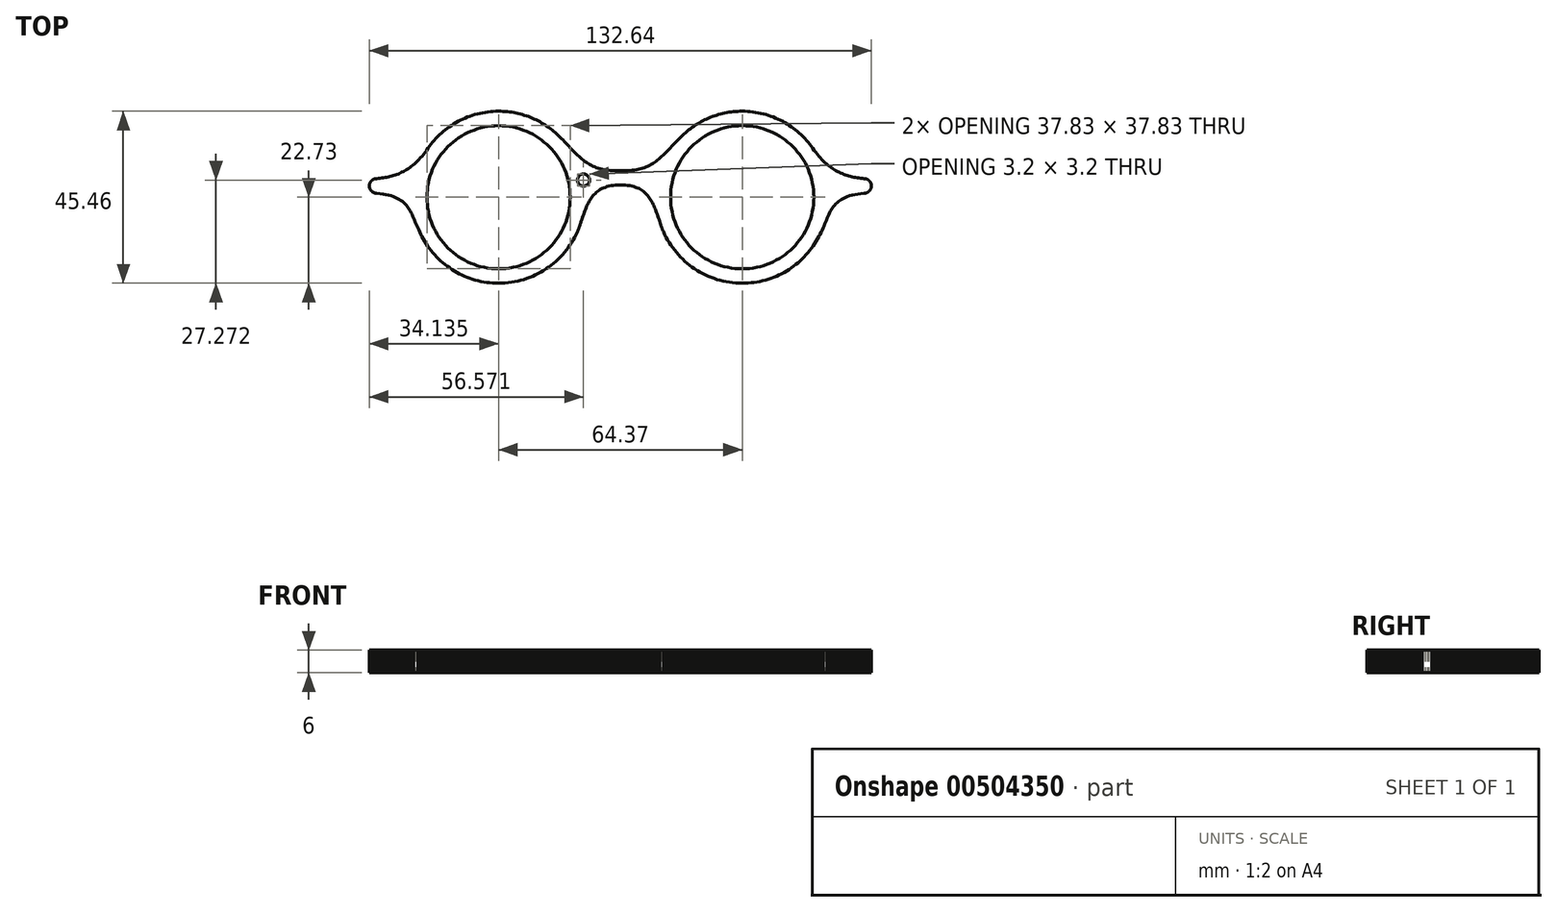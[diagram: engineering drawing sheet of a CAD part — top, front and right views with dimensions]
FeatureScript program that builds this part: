
annotation { "Feature Type Name" : "Feature", "Feature Type Description" : "" }
export const myFeature = defineFeature(function(context is Context, id is Id, definition is map)
    precondition{}
    {
        {
            var Q0;
            Q0=qCreatedBy(makeId("Top.planeOp"),FACE);
            var sketch = newSketch(context, id + "F0", { "sketchPlane" : qUnion([Q0])});
            skLineSegment(sketch, "E0", {"start": v(66.32, 3.1) * mm, "end": v(66.3, 3.2) * mm});
            skLineSegment(sketch, "E1", {"start": v(66.3, 3.2) * mm, "end": v(66.3, 3.3) * mm});
            skLineSegment(sketch, "E2", {"start": v(66.3, 3.3) * mm, "end": v(66.28, 3.39) * mm});
            skLineSegment(sketch, "E3", {"start": v(66.28, 3.39) * mm, "end": v(66.26, 3.48) * mm});
            skLineSegment(sketch, "E4", {"start": v(66.26, 3.48) * mm, "end": v(66.23, 3.57) * mm});
            skLineSegment(sketch, "E5", {"start": v(66.23, 3.57) * mm, "end": v(66.2, 3.66) * mm});
            skLineSegment(sketch, "E6", {"start": v(66.2, 3.66) * mm, "end": v(66.17, 3.75) * mm});
            skLineSegment(sketch, "E7", {"start": v(66.17, 3.75) * mm, "end": v(66.13, 3.84) * mm});
            skLineSegment(sketch, "E8", {"start": v(66.13, 3.84) * mm, "end": v(66.08, 3.92) * mm});
            skLineSegment(sketch, "E9", {"start": v(66.08, 3.92) * mm, "end": v(66.04, 4) * mm});
            skLineSegment(sketch, "E10", {"start": v(66.04, 4) * mm, "end": v(65.99, 4.08) * mm});
            skLineSegment(sketch, "E11", {"start": v(65.99, 4.08) * mm, "end": v(65.93, 4.16) * mm});
            skLineSegment(sketch, "E12", {"start": v(65.93, 4.16) * mm, "end": v(65.88, 4.23) * mm});
            skLineSegment(sketch, "E13", {"start": v(65.88, 4.23) * mm, "end": v(65.82, 4.3) * mm});
            skLineSegment(sketch, "E14", {"start": v(65.82, 4.3) * mm, "end": v(65.75, 4.37) * mm});
            skLineSegment(sketch, "E15", {"start": v(65.75, 4.37) * mm, "end": v(65.69, 4.43) * mm});
            skLineSegment(sketch, "E16", {"start": v(65.69, 4.43) * mm, "end": v(65.62, 4.5) * mm});
            skLineSegment(sketch, "E17", {"start": v(65.62, 4.5) * mm, "end": v(65.54, 4.55) * mm});
            skLineSegment(sketch, "E18", {"start": v(65.54, 4.55) * mm, "end": v(65.47, 4.6) * mm});
            skLineSegment(sketch, "E19", {"start": v(65.47, 4.6) * mm, "end": v(65.39, 4.65) * mm});
            skLineSegment(sketch, "E20", {"start": v(65.39, 4.65) * mm, "end": v(65.3, 4.7) * mm});
            skLineSegment(sketch, "E21", {"start": v(65.3, 4.7) * mm, "end": v(65.22, 4.74) * mm});
            skLineSegment(sketch, "E22", {"start": v(65.22, 4.74) * mm, "end": v(65.14, 4.78) * mm});
            skLineSegment(sketch, "E23", {"start": v(65.14, 4.78) * mm, "end": v(65.05, 4.81) * mm});
            skLineSegment(sketch, "E24", {"start": v(65.05, 4.81) * mm, "end": v(64.96, 4.84) * mm});
            skLineSegment(sketch, "E25", {"start": v(64.96, 4.84) * mm, "end": v(64.87, 4.87) * mm});
            skLineSegment(sketch, "E26", {"start": v(64.87, 4.87) * mm, "end": v(64.78, 4.9) * mm});
            skLineSegment(sketch, "E27", {"start": v(64.78, 4.9) * mm, "end": v(64.68, 4.9) * mm});
            skLineSegment(sketch, "E28", {"start": v(64.68, 4.9) * mm, "end": v(64.58, 4.92) * mm});
            skLineSegment(sketch, "E29", {"start": v(64.58, 4.92) * mm, "end": v(64.49, 4.93) * mm});
            skLineSegment(sketch, "E30", {"start": v(64.49, 4.93) * mm, "end": v(64.39, 4.93) * mm});
            skLineSegment(sketch, "E31", {"start": v(64.39, 4.93) * mm, "end": v(63.93, 4.97) * mm});
            skLineSegment(sketch, "E32", {"start": v(63.93, 4.97) * mm, "end": v(63.48, 5.02) * mm});
            skLineSegment(sketch, "E33", {"start": v(63.48, 5.02) * mm, "end": v(63.03, 5.07) * mm});
            skLineSegment(sketch, "E34", {"start": v(63.03, 5.07) * mm, "end": v(62.58, 5.14) * mm});
            skLineSegment(sketch, "E35", {"start": v(62.58, 5.14) * mm, "end": v(62.13, 5.21) * mm});
            skLineSegment(sketch, "E36", {"start": v(62.13, 5.21) * mm, "end": v(61.68, 5.3) * mm});
            skLineSegment(sketch, "E37", {"start": v(61.68, 5.3) * mm, "end": v(61.24, 5.4) * mm});
            skLineSegment(sketch, "E38", {"start": v(61.24, 5.4) * mm, "end": v(60.8, 5.5) * mm});
            skLineSegment(sketch, "E39", {"start": v(60.8, 5.5) * mm, "end": v(60.36, 5.61) * mm});
            skLineSegment(sketch, "E40", {"start": v(60.36, 5.61) * mm, "end": v(59.92, 5.74) * mm});
            skLineSegment(sketch, "E41", {"start": v(59.92, 5.74) * mm, "end": v(59.48, 5.89) * mm});
            skLineSegment(sketch, "E42", {"start": v(59.48, 5.89) * mm, "end": v(59.04, 6.04) * mm});
            skLineSegment(sketch, "E43", {"start": v(59.04, 6.04) * mm, "end": v(58.61, 6.22) * mm});
            skLineSegment(sketch, "E44", {"start": v(58.61, 6.22) * mm, "end": v(58.18, 6.4) * mm});
            skLineSegment(sketch, "E45", {"start": v(58.18, 6.4) * mm, "end": v(57.75, 6.6) * mm});
            skLineSegment(sketch, "E46", {"start": v(57.75, 6.6) * mm, "end": v(57.32, 6.82) * mm});
            skLineSegment(sketch, "E47", {"start": v(57.32, 6.82) * mm, "end": v(56.9, 7.06) * mm});
            skLineSegment(sketch, "E48", {"start": v(56.9, 7.06) * mm, "end": v(56.48, 7.3) * mm});
            skLineSegment(sketch, "E49", {"start": v(56.48, 7.3) * mm, "end": v(56.06, 7.58) * mm});
            skLineSegment(sketch, "E50", {"start": v(56.06, 7.58) * mm, "end": v(55.64, 7.86) * mm});
            skLineSegment(sketch, "E51", {"start": v(55.64, 7.86) * mm, "end": v(55.23, 8.17) * mm});
            skLineSegment(sketch, "E52", {"start": v(55.23, 8.17) * mm, "end": v(54.81, 8.5) * mm});
            skLineSegment(sketch, "E53", {"start": v(54.81, 8.5) * mm, "end": v(54.4, 8.84) * mm});
            skLineSegment(sketch, "E54", {"start": v(54.4, 8.84) * mm, "end": v(54, 9.21) * mm});
            skLineSegment(sketch, "E55", {"start": v(54, 9.21) * mm, "end": v(53.6, 9.6) * mm});
            skLineSegment(sketch, "E56", {"start": v(53.6, 9.6) * mm, "end": v(53.2, 10) * mm});
            skLineSegment(sketch, "E57", {"start": v(53.2, 10) * mm, "end": v(52.8, 10.44) * mm});
            skLineSegment(sketch, "E58", {"start": v(52.8, 10.44) * mm, "end": v(52.4, 10.9) * mm});
            skLineSegment(sketch, "E59", {"start": v(52.4, 10.9) * mm, "end": v(52, 11.38) * mm});
            skLineSegment(sketch, "E60", {"start": v(52, 11.38) * mm, "end": v(51.61, 11.88) * mm});
            skLineSegment(sketch, "E61", {"start": v(51.61, 11.88) * mm, "end": v(51.23, 12.41) * mm});
            skLineSegment(sketch, "E62", {"start": v(51.23, 12.41) * mm, "end": v(50.84, 12.97) * mm});
            skLineSegment(sketch, "E63", {"start": v(50.84, 12.97) * mm, "end": v(50.45, 13.51) * mm});
            skLineSegment(sketch, "E64", {"start": v(50.45, 13.51) * mm, "end": v(50.04, 14.05) * mm});
            skLineSegment(sketch, "E65", {"start": v(50.04, 14.05) * mm, "end": v(49.62, 14.57) * mm});
            skLineSegment(sketch, "E66", {"start": v(49.62, 14.57) * mm, "end": v(49.18, 15.08) * mm});
            skLineSegment(sketch, "E67", {"start": v(49.18, 15.08) * mm, "end": v(48.72, 15.58) * mm});
            skLineSegment(sketch, "E68", {"start": v(48.72, 15.58) * mm, "end": v(48.26, 16.06) * mm});
            skLineSegment(sketch, "E69", {"start": v(48.26, 16.06) * mm, "end": v(47.77, 16.53) * mm});
            skLineSegment(sketch, "E70", {"start": v(47.77, 16.53) * mm, "end": v(47.28, 16.98) * mm});
            skLineSegment(sketch, "E71", {"start": v(47.28, 16.98) * mm, "end": v(46.77, 17.42) * mm});
            skLineSegment(sketch, "E72", {"start": v(46.77, 17.42) * mm, "end": v(46.25, 17.85) * mm});
            skLineSegment(sketch, "E73", {"start": v(46.25, 17.85) * mm, "end": v(45.71, 18.26) * mm});
            skLineSegment(sketch, "E74", {"start": v(45.71, 18.26) * mm, "end": v(45.17, 18.65) * mm});
            skLineSegment(sketch, "E75", {"start": v(45.17, 18.65) * mm, "end": v(44.6, 19.03) * mm});
            skLineSegment(sketch, "E76", {"start": v(44.6, 19.03) * mm, "end": v(44.04, 19.39) * mm});
            skLineSegment(sketch, "E77", {"start": v(44.04, 19.39) * mm, "end": v(43.46, 19.73) * mm});
            skLineSegment(sketch, "E78", {"start": v(43.46, 19.73) * mm, "end": v(42.87, 20.06) * mm});
            skLineSegment(sketch, "E79", {"start": v(42.87, 20.06) * mm, "end": v(42.26, 20.37) * mm});
            skLineSegment(sketch, "E80", {"start": v(42.26, 20.37) * mm, "end": v(41.65, 20.67) * mm});
            skLineSegment(sketch, "E81", {"start": v(41.65, 20.67) * mm, "end": v(41.03, 20.94) * mm});
            skLineSegment(sketch, "E82", {"start": v(41.03, 20.94) * mm, "end": v(40.4, 21.2) * mm});
            skLineSegment(sketch, "E83", {"start": v(40.4, 21.2) * mm, "end": v(39.75, 21.44) * mm});
            skLineSegment(sketch, "E84", {"start": v(39.75, 21.44) * mm, "end": v(39.1, 21.66) * mm});
            skLineSegment(sketch, "E85", {"start": v(39.1, 21.66) * mm, "end": v(38.45, 21.86) * mm});
            skLineSegment(sketch, "E86", {"start": v(38.45, 21.86) * mm, "end": v(37.78, 22.04) * mm});
            skLineSegment(sketch, "E87", {"start": v(37.78, 22.04) * mm, "end": v(37.1, 22.2) * mm});
            skLineSegment(sketch, "E88", {"start": v(37.1, 22.2) * mm, "end": v(36.42, 22.34) * mm});
            skLineSegment(sketch, "E89", {"start": v(36.42, 22.34) * mm, "end": v(35.73, 22.46) * mm});
            skLineSegment(sketch, "E90", {"start": v(35.73, 22.46) * mm, "end": v(35.03, 22.56) * mm});
            skLineSegment(sketch, "E91", {"start": v(35.03, 22.56) * mm, "end": v(34.33, 22.63) * mm});
            skLineSegment(sketch, "E92", {"start": v(34.33, 22.63) * mm, "end": v(33.62, 22.69) * mm});
            skLineSegment(sketch, "E93", {"start": v(33.62, 22.69) * mm, "end": v(32.9, 22.72) * mm});
            skLineSegment(sketch, "E94", {"start": v(32.9, 22.72) * mm, "end": v(32.19, 22.73) * mm});
            skLineSegment(sketch, "E95", {"start": v(32.19, 22.73) * mm, "end": v(31.6, 22.73) * mm});
            skLineSegment(sketch, "E96", {"start": v(31.6, 22.73) * mm, "end": v(31, 22.7) * mm});
            skLineSegment(sketch, "E97", {"start": v(31, 22.7) * mm, "end": v(30.42, 22.67) * mm});
            skLineSegment(sketch, "E98", {"start": v(30.42, 22.67) * mm, "end": v(29.84, 22.61) * mm});
            skLineSegment(sketch, "E99", {"start": v(29.84, 22.61) * mm, "end": v(29.27, 22.55) * mm});
            skLineSegment(sketch, "E100", {"start": v(29.27, 22.55) * mm, "end": v(28.7, 22.47) * mm});
            skLineSegment(sketch, "E101", {"start": v(28.7, 22.47) * mm, "end": v(28.13, 22.37) * mm});
            skLineSegment(sketch, "E102", {"start": v(28.13, 22.37) * mm, "end": v(27.57, 22.26) * mm});
            skLineSegment(sketch, "E103", {"start": v(27.57, 22.26) * mm, "end": v(27.01, 22.14) * mm});
            skLineSegment(sketch, "E104", {"start": v(27.01, 22.14) * mm, "end": v(26.46, 22) * mm});
            skLineSegment(sketch, "E105", {"start": v(26.46, 22) * mm, "end": v(25.92, 21.85) * mm});
            skLineSegment(sketch, "E106", {"start": v(25.92, 21.85) * mm, "end": v(25.38, 21.7) * mm});
            skLineSegment(sketch, "E107", {"start": v(25.38, 21.7) * mm, "end": v(24.84, 21.52) * mm});
            skLineSegment(sketch, "E108", {"start": v(24.84, 21.52) * mm, "end": v(24.31, 21.33) * mm});
            skLineSegment(sketch, "E109", {"start": v(24.31, 21.33) * mm, "end": v(23.8, 21.13) * mm});
            skLineSegment(sketch, "E110", {"start": v(23.8, 21.13) * mm, "end": v(23.28, 20.91) * mm});
            skLineSegment(sketch, "E111", {"start": v(23.28, 20.91) * mm, "end": v(22.77, 20.69) * mm});
            skLineSegment(sketch, "E112", {"start": v(22.77, 20.69) * mm, "end": v(22.26, 20.45) * mm});
            skLineSegment(sketch, "E113", {"start": v(22.26, 20.45) * mm, "end": v(21.77, 20.2) * mm});
            skLineSegment(sketch, "E114", {"start": v(21.77, 20.2) * mm, "end": v(21.28, 19.94) * mm});
            skLineSegment(sketch, "E115", {"start": v(21.28, 19.94) * mm, "end": v(20.8, 19.67) * mm});
            skLineSegment(sketch, "E116", {"start": v(20.8, 19.67) * mm, "end": v(20.32, 19.38) * mm});
            skLineSegment(sketch, "E117", {"start": v(20.32, 19.38) * mm, "end": v(19.85, 19.09) * mm});
            skLineSegment(sketch, "E118", {"start": v(19.85, 19.09) * mm, "end": v(19.4, 18.78) * mm});
            skLineSegment(sketch, "E119", {"start": v(19.4, 18.78) * mm, "end": v(18.94, 18.46) * mm});
            skLineSegment(sketch, "E120", {"start": v(18.94, 18.46) * mm, "end": v(18.5, 18.14) * mm});
            skLineSegment(sketch, "E121", {"start": v(18.5, 18.14) * mm, "end": v(18.06, 17.8) * mm});
            skLineSegment(sketch, "E122", {"start": v(18.06, 17.8) * mm, "end": v(17.63, 17.45) * mm});
            skLineSegment(sketch, "E123", {"start": v(17.63, 17.45) * mm, "end": v(17.21, 17.1) * mm});
            skLineSegment(sketch, "E124", {"start": v(17.21, 17.1) * mm, "end": v(16.8, 16.72) * mm});
            skLineSegment(sketch, "E125", {"start": v(16.8, 16.72) * mm, "end": v(16.4, 16.35) * mm});
            skLineSegment(sketch, "E126", {"start": v(16.4, 16.35) * mm, "end": v(16.01, 15.96) * mm});
            skLineSegment(sketch, "E127", {"start": v(16.01, 15.96) * mm, "end": v(15.58, 15.53) * mm});
            skLineSegment(sketch, "E128", {"start": v(15.58, 15.53) * mm, "end": v(15.16, 15.11) * mm});
            skLineSegment(sketch, "E129", {"start": v(15.16, 15.11) * mm, "end": v(14.75, 14.7) * mm});
            skLineSegment(sketch, "E130", {"start": v(14.75, 14.7) * mm, "end": v(14.35, 14.27) * mm});
            skLineSegment(sketch, "E131", {"start": v(14.35, 14.27) * mm, "end": v(13.96, 13.86) * mm});
            skLineSegment(sketch, "E132", {"start": v(13.96, 13.86) * mm, "end": v(13.57, 13.45) * mm});
            skLineSegment(sketch, "E133", {"start": v(13.57, 13.45) * mm, "end": v(13.18, 13.05) * mm});
            skLineSegment(sketch, "E134", {"start": v(13.18, 13.05) * mm, "end": v(12.8, 12.66) * mm});
            skLineSegment(sketch, "E135", {"start": v(12.8, 12.66) * mm, "end": v(12.43, 12.27) * mm});
            skLineSegment(sketch, "E136", {"start": v(12.43, 12.27) * mm, "end": v(12.05, 11.89) * mm});
            skLineSegment(sketch, "E137", {"start": v(12.05, 11.89) * mm, "end": v(11.68, 11.52) * mm});
            skLineSegment(sketch, "E138", {"start": v(11.68, 11.52) * mm, "end": v(11.3, 11.15) * mm});
            skLineSegment(sketch, "E139", {"start": v(11.3, 11.15) * mm, "end": v(10.92, 10.8) * mm});
            skLineSegment(sketch, "E140", {"start": v(10.92, 10.8) * mm, "end": v(10.54, 10.46) * mm});
            skLineSegment(sketch, "E141", {"start": v(10.54, 10.46) * mm, "end": v(10.16, 10.13) * mm});
            skLineSegment(sketch, "E142", {"start": v(10.16, 10.13) * mm, "end": v(9.77, 9.81) * mm});
            skLineSegment(sketch, "E143", {"start": v(9.77, 9.81) * mm, "end": v(9.37, 9.5) * mm});
            skLineSegment(sketch, "E144", {"start": v(9.37, 9.5) * mm, "end": v(8.97, 9.22) * mm});
            skLineSegment(sketch, "E145", {"start": v(8.97, 9.22) * mm, "end": v(8.55, 8.94) * mm});
            skLineSegment(sketch, "E146", {"start": v(8.55, 8.94) * mm, "end": v(8.13, 8.68) * mm});
            skLineSegment(sketch, "E147", {"start": v(8.13, 8.68) * mm, "end": v(7.7, 8.44) * mm});
            skLineSegment(sketch, "E148", {"start": v(7.7, 8.44) * mm, "end": v(7.25, 8.22) * mm});
            skLineSegment(sketch, "E149", {"start": v(7.25, 8.22) * mm, "end": v(6.8, 8) * mm});
            skLineSegment(sketch, "E150", {"start": v(6.8, 8) * mm, "end": v(6.32, 7.82) * mm});
            skLineSegment(sketch, "E151", {"start": v(6.32, 7.82) * mm, "end": v(5.84, 7.65) * mm});
            skLineSegment(sketch, "E152", {"start": v(5.84, 7.65) * mm, "end": v(5.33, 7.5) * mm});
            skLineSegment(sketch, "E153", {"start": v(5.33, 7.5) * mm, "end": v(4.81, 7.37) * mm});
            skLineSegment(sketch, "E154", {"start": v(4.81, 7.37) * mm, "end": v(4.27, 7.26) * mm});
            skLineSegment(sketch, "E155", {"start": v(4.27, 7.26) * mm, "end": v(3.71, 7.18) * mm});
            skLineSegment(sketch, "E156", {"start": v(3.71, 7.18) * mm, "end": v(3.13, 7.12) * mm});
            skLineSegment(sketch, "E157", {"start": v(3.13, 7.12) * mm, "end": v(2.53, 7.08) * mm});
            skLineSegment(sketch, "E158", {"start": v(2.53, 7.08) * mm, "end": v(1.9, 7.07) * mm});
            skLineSegment(sketch, "E159", {"start": v(1.9, 7.07) * mm, "end": v(0, 7.07) * mm});
            skLineSegment(sketch, "E160", {"start": v(0, 7.07) * mm, "end": v(-1.9, 7.07) * mm});
            skLineSegment(sketch, "E161", {"start": v(-1.9, 7.07) * mm, "end": v(-2.52, 7.08) * mm});
            skLineSegment(sketch, "E162", {"start": v(-2.52, 7.08) * mm, "end": v(-3.13, 7.12) * mm});
            skLineSegment(sketch, "E163", {"start": v(-3.13, 7.12) * mm, "end": v(-3.71, 7.18) * mm});
            skLineSegment(sketch, "E164", {"start": v(-3.71, 7.18) * mm, "end": v(-4.27, 7.26) * mm});
            skLineSegment(sketch, "E165", {"start": v(-4.27, 7.26) * mm, "end": v(-4.81, 7.37) * mm});
            skLineSegment(sketch, "E166", {"start": v(-4.81, 7.37) * mm, "end": v(-5.33, 7.5) * mm});
            skLineSegment(sketch, "E167", {"start": v(-5.33, 7.5) * mm, "end": v(-5.84, 7.65) * mm});
            skLineSegment(sketch, "E168", {"start": v(-5.84, 7.65) * mm, "end": v(-6.32, 7.82) * mm});
            skLineSegment(sketch, "E169", {"start": v(-6.32, 7.82) * mm, "end": v(-6.8, 8) * mm});
            skLineSegment(sketch, "E170", {"start": v(-6.8, 8) * mm, "end": v(-7.25, 8.22) * mm});
            skLineSegment(sketch, "E171", {"start": v(-7.25, 8.22) * mm, "end": v(-7.7, 8.44) * mm});
            skLineSegment(sketch, "E172", {"start": v(-7.7, 8.44) * mm, "end": v(-8.13, 8.68) * mm});
            skLineSegment(sketch, "E173", {"start": v(-8.13, 8.68) * mm, "end": v(-8.55, 8.94) * mm});
            skLineSegment(sketch, "E174", {"start": v(-8.55, 8.94) * mm, "end": v(-8.97, 9.22) * mm});
            skLineSegment(sketch, "E175", {"start": v(-8.97, 9.22) * mm, "end": v(-9.37, 9.5) * mm});
            skLineSegment(sketch, "E176", {"start": v(-9.37, 9.5) * mm, "end": v(-9.77, 9.81) * mm});
            skLineSegment(sketch, "E177", {"start": v(-9.77, 9.81) * mm, "end": v(-10.16, 10.13) * mm});
            skLineSegment(sketch, "E178", {"start": v(-10.16, 10.13) * mm, "end": v(-10.54, 10.46) * mm});
            skLineSegment(sketch, "E179", {"start": v(-10.54, 10.46) * mm, "end": v(-10.92, 10.8) * mm});
            skLineSegment(sketch, "E180", {"start": v(-10.92, 10.8) * mm, "end": v(-11.3, 11.15) * mm});
            skLineSegment(sketch, "E181", {"start": v(-11.3, 11.15) * mm, "end": v(-11.68, 11.52) * mm});
            skLineSegment(sketch, "E182", {"start": v(-11.68, 11.52) * mm, "end": v(-12.05, 11.89) * mm});
            skLineSegment(sketch, "E183", {"start": v(-12.05, 11.89) * mm, "end": v(-12.43, 12.27) * mm});
            skLineSegment(sketch, "E184", {"start": v(-12.43, 12.27) * mm, "end": v(-12.8, 12.66) * mm});
            skLineSegment(sketch, "E185", {"start": v(-12.8, 12.66) * mm, "end": v(-13.18, 13.05) * mm});
            skLineSegment(sketch, "E186", {"start": v(-13.18, 13.05) * mm, "end": v(-13.57, 13.45) * mm});
            skLineSegment(sketch, "E187", {"start": v(-13.57, 13.45) * mm, "end": v(-13.96, 13.86) * mm});
            skLineSegment(sketch, "E188", {"start": v(-13.96, 13.86) * mm, "end": v(-14.35, 14.27) * mm});
            skLineSegment(sketch, "E189", {"start": v(-14.35, 14.27) * mm, "end": v(-14.75, 14.7) * mm});
            skLineSegment(sketch, "E190", {"start": v(-14.75, 14.7) * mm, "end": v(-15.16, 15.11) * mm});
            skLineSegment(sketch, "E191", {"start": v(-15.16, 15.11) * mm, "end": v(-15.58, 15.53) * mm});
            skLineSegment(sketch, "E192", {"start": v(-15.58, 15.53) * mm, "end": v(-16.01, 15.96) * mm});
            skLineSegment(sketch, "E193", {"start": v(-16.01, 15.96) * mm, "end": v(-16.4, 16.35) * mm});
            skLineSegment(sketch, "E194", {"start": v(-16.4, 16.35) * mm, "end": v(-16.8, 16.72) * mm});
            skLineSegment(sketch, "E195", {"start": v(-16.8, 16.72) * mm, "end": v(-17.21, 17.1) * mm});
            skLineSegment(sketch, "E196", {"start": v(-17.21, 17.1) * mm, "end": v(-17.63, 17.45) * mm});
            skLineSegment(sketch, "E197", {"start": v(-17.63, 17.45) * mm, "end": v(-18.06, 17.8) * mm});
            skLineSegment(sketch, "E198", {"start": v(-18.06, 17.8) * mm, "end": v(-18.5, 18.14) * mm});
            skLineSegment(sketch, "E199", {"start": v(-18.5, 18.14) * mm, "end": v(-18.94, 18.46) * mm});
            skLineSegment(sketch, "E200", {"start": v(-18.94, 18.46) * mm, "end": v(-19.4, 18.78) * mm});
            skLineSegment(sketch, "E201", {"start": v(-19.4, 18.78) * mm, "end": v(-19.85, 19.09) * mm});
            skLineSegment(sketch, "E202", {"start": v(-19.85, 19.09) * mm, "end": v(-20.32, 19.38) * mm});
            skLineSegment(sketch, "E203", {"start": v(-20.32, 19.38) * mm, "end": v(-20.8, 19.67) * mm});
            skLineSegment(sketch, "E204", {"start": v(-20.8, 19.67) * mm, "end": v(-21.28, 19.94) * mm});
            skLineSegment(sketch, "E205", {"start": v(-21.28, 19.94) * mm, "end": v(-21.77, 20.2) * mm});
            skLineSegment(sketch, "E206", {"start": v(-21.77, 20.2) * mm, "end": v(-22.26, 20.45) * mm});
            skLineSegment(sketch, "E207", {"start": v(-22.26, 20.45) * mm, "end": v(-22.76, 20.69) * mm});
            skLineSegment(sketch, "E208", {"start": v(-22.76, 20.69) * mm, "end": v(-23.27, 20.91) * mm});
            skLineSegment(sketch, "E209", {"start": v(-23.27, 20.91) * mm, "end": v(-23.8, 21.13) * mm});
            skLineSegment(sketch, "E210", {"start": v(-23.8, 21.13) * mm, "end": v(-24.31, 21.33) * mm});
            skLineSegment(sketch, "E211", {"start": v(-24.31, 21.33) * mm, "end": v(-24.84, 21.52) * mm});
            skLineSegment(sketch, "E212", {"start": v(-24.84, 21.52) * mm, "end": v(-25.38, 21.7) * mm});
            skLineSegment(sketch, "E213", {"start": v(-25.38, 21.7) * mm, "end": v(-25.92, 21.85) * mm});
            skLineSegment(sketch, "E214", {"start": v(-25.92, 21.85) * mm, "end": v(-26.46, 22) * mm});
            skLineSegment(sketch, "E215", {"start": v(-26.46, 22) * mm, "end": v(-27.01, 22.14) * mm});
            skLineSegment(sketch, "E216", {"start": v(-27.01, 22.14) * mm, "end": v(-27.57, 22.26) * mm});
            skLineSegment(sketch, "E217", {"start": v(-27.57, 22.26) * mm, "end": v(-28.13, 22.37) * mm});
            skLineSegment(sketch, "E218", {"start": v(-28.13, 22.37) * mm, "end": v(-28.7, 22.47) * mm});
            skLineSegment(sketch, "E219", {"start": v(-28.7, 22.47) * mm, "end": v(-29.27, 22.55) * mm});
            skLineSegment(sketch, "E220", {"start": v(-29.27, 22.55) * mm, "end": v(-29.84, 22.61) * mm});
            skLineSegment(sketch, "E221", {"start": v(-29.84, 22.61) * mm, "end": v(-30.42, 22.67) * mm});
            skLineSegment(sketch, "E222", {"start": v(-30.42, 22.67) * mm, "end": v(-31, 22.7) * mm});
            skLineSegment(sketch, "E223", {"start": v(-31, 22.7) * mm, "end": v(-31.6, 22.73) * mm});
            skLineSegment(sketch, "E224", {"start": v(-31.6, 22.73) * mm, "end": v(-32.19, 22.73) * mm});
            skLineSegment(sketch, "E225", {"start": v(-32.19, 22.73) * mm, "end": v(-32.9, 22.72) * mm});
            skLineSegment(sketch, "E226", {"start": v(-32.9, 22.72) * mm, "end": v(-33.62, 22.69) * mm});
            skLineSegment(sketch, "E227", {"start": v(-33.62, 22.69) * mm, "end": v(-34.33, 22.63) * mm});
            skLineSegment(sketch, "E228", {"start": v(-34.33, 22.63) * mm, "end": v(-35.03, 22.56) * mm});
            skLineSegment(sketch, "E229", {"start": v(-35.03, 22.56) * mm, "end": v(-35.73, 22.46) * mm});
            skLineSegment(sketch, "E230", {"start": v(-35.73, 22.46) * mm, "end": v(-36.42, 22.34) * mm});
            skLineSegment(sketch, "E231", {"start": v(-36.42, 22.34) * mm, "end": v(-37.1, 22.2) * mm});
            skLineSegment(sketch, "E232", {"start": v(-37.1, 22.2) * mm, "end": v(-37.78, 22.04) * mm});
            skLineSegment(sketch, "E233", {"start": v(-37.78, 22.04) * mm, "end": v(-38.45, 21.86) * mm});
            skLineSegment(sketch, "E234", {"start": v(-38.45, 21.86) * mm, "end": v(-39.1, 21.66) * mm});
            skLineSegment(sketch, "E235", {"start": v(-39.1, 21.66) * mm, "end": v(-39.75, 21.44) * mm});
            skLineSegment(sketch, "E236", {"start": v(-39.75, 21.44) * mm, "end": v(-40.4, 21.2) * mm});
            skLineSegment(sketch, "E237", {"start": v(-40.4, 21.2) * mm, "end": v(-41.03, 20.94) * mm});
            skLineSegment(sketch, "E238", {"start": v(-41.03, 20.94) * mm, "end": v(-41.65, 20.67) * mm});
            skLineSegment(sketch, "E239", {"start": v(-41.65, 20.67) * mm, "end": v(-42.26, 20.37) * mm});
            skLineSegment(sketch, "E240", {"start": v(-42.26, 20.37) * mm, "end": v(-42.87, 20.06) * mm});
            skLineSegment(sketch, "E241", {"start": v(-42.87, 20.06) * mm, "end": v(-43.46, 19.73) * mm});
            skLineSegment(sketch, "E242", {"start": v(-43.46, 19.73) * mm, "end": v(-44.04, 19.39) * mm});
            skLineSegment(sketch, "E243", {"start": v(-44.04, 19.39) * mm, "end": v(-44.6, 19.03) * mm});
            skLineSegment(sketch, "E244", {"start": v(-44.6, 19.03) * mm, "end": v(-45.17, 18.65) * mm});
            skLineSegment(sketch, "E245", {"start": v(-45.17, 18.65) * mm, "end": v(-45.71, 18.26) * mm});
            skLineSegment(sketch, "E246", {"start": v(-45.71, 18.26) * mm, "end": v(-46.25, 17.85) * mm});
            skLineSegment(sketch, "E247", {"start": v(-46.25, 17.85) * mm, "end": v(-46.77, 17.42) * mm});
            skLineSegment(sketch, "E248", {"start": v(-46.77, 17.42) * mm, "end": v(-47.28, 16.98) * mm});
            skLineSegment(sketch, "E249", {"start": v(-47.28, 16.98) * mm, "end": v(-47.77, 16.53) * mm});
            skLineSegment(sketch, "E250", {"start": v(-47.77, 16.53) * mm, "end": v(-48.25, 16.06) * mm});
            skLineSegment(sketch, "E251", {"start": v(-48.25, 16.06) * mm, "end": v(-48.72, 15.58) * mm});
            skLineSegment(sketch, "E252", {"start": v(-48.72, 15.58) * mm, "end": v(-49.18, 15.08) * mm});
            skLineSegment(sketch, "E253", {"start": v(-49.18, 15.08) * mm, "end": v(-49.62, 14.57) * mm});
            skLineSegment(sketch, "E254", {"start": v(-49.62, 14.57) * mm, "end": v(-50.04, 14.05) * mm});
            skLineSegment(sketch, "E255", {"start": v(-50.04, 14.05) * mm, "end": v(-50.45, 13.51) * mm});
            skLineSegment(sketch, "E256", {"start": v(-50.45, 13.51) * mm, "end": v(-50.84, 12.97) * mm});
            skLineSegment(sketch, "E257", {"start": v(-50.84, 12.97) * mm, "end": v(-51.23, 12.41) * mm});
            skLineSegment(sketch, "E258", {"start": v(-51.23, 12.41) * mm, "end": v(-51.61, 11.88) * mm});
            skLineSegment(sketch, "E259", {"start": v(-51.61, 11.88) * mm, "end": v(-52, 11.38) * mm});
            skLineSegment(sketch, "E260", {"start": v(-52, 11.38) * mm, "end": v(-52.4, 10.9) * mm});
            skLineSegment(sketch, "E261", {"start": v(-52.4, 10.9) * mm, "end": v(-52.8, 10.44) * mm});
            skLineSegment(sketch, "E262", {"start": v(-52.8, 10.44) * mm, "end": v(-53.2, 10) * mm});
            skLineSegment(sketch, "E263", {"start": v(-53.2, 10) * mm, "end": v(-53.6, 9.6) * mm});
            skLineSegment(sketch, "E264", {"start": v(-53.6, 9.6) * mm, "end": v(-54, 9.2) * mm});
            skLineSegment(sketch, "E265", {"start": v(-54, 9.2) * mm, "end": v(-54.4, 8.84) * mm});
            skLineSegment(sketch, "E266", {"start": v(-54.4, 8.84) * mm, "end": v(-54.82, 8.5) * mm});
            skLineSegment(sketch, "E267", {"start": v(-54.82, 8.5) * mm, "end": v(-55.23, 8.17) * mm});
            skLineSegment(sketch, "E268", {"start": v(-55.23, 8.17) * mm, "end": v(-55.64, 7.86) * mm});
            skLineSegment(sketch, "E269", {"start": v(-55.64, 7.86) * mm, "end": v(-56.06, 7.57) * mm});
            skLineSegment(sketch, "E270", {"start": v(-56.06, 7.57) * mm, "end": v(-56.48, 7.3) * mm});
            skLineSegment(sketch, "E271", {"start": v(-56.48, 7.3) * mm, "end": v(-56.9, 7.05) * mm});
            skLineSegment(sketch, "E272", {"start": v(-56.9, 7.05) * mm, "end": v(-57.33, 6.82) * mm});
            skLineSegment(sketch, "E273", {"start": v(-57.33, 6.82) * mm, "end": v(-57.76, 6.6) * mm});
            skLineSegment(sketch, "E274", {"start": v(-57.76, 6.6) * mm, "end": v(-58.19, 6.4) * mm});
            skLineSegment(sketch, "E275", {"start": v(-58.19, 6.4) * mm, "end": v(-58.62, 6.2) * mm});
            skLineSegment(sketch, "E276", {"start": v(-58.62, 6.2) * mm, "end": v(-59.05, 6.04) * mm});
            skLineSegment(sketch, "E277", {"start": v(-59.05, 6.04) * mm, "end": v(-59.49, 5.88) * mm});
            skLineSegment(sketch, "E278", {"start": v(-59.49, 5.88) * mm, "end": v(-59.93, 5.74) * mm});
            skLineSegment(sketch, "E279", {"start": v(-59.93, 5.74) * mm, "end": v(-60.36, 5.6) * mm});
            skLineSegment(sketch, "E280", {"start": v(-60.36, 5.6) * mm, "end": v(-60.8, 5.49) * mm});
            skLineSegment(sketch, "E281", {"start": v(-60.8, 5.49) * mm, "end": v(-61.25, 5.38) * mm});
            skLineSegment(sketch, "E282", {"start": v(-61.25, 5.38) * mm, "end": v(-61.7, 5.29) * mm});
            skLineSegment(sketch, "E283", {"start": v(-61.7, 5.29) * mm, "end": v(-62.14, 5.2) * mm});
            skLineSegment(sketch, "E284", {"start": v(-62.14, 5.2) * mm, "end": v(-62.58, 5.13) * mm});
            skLineSegment(sketch, "E285", {"start": v(-62.58, 5.13) * mm, "end": v(-63.03, 5.07) * mm});
            skLineSegment(sketch, "E286", {"start": v(-63.03, 5.07) * mm, "end": v(-63.48, 5.01) * mm});
            skLineSegment(sketch, "E287", {"start": v(-63.48, 5.01) * mm, "end": v(-63.93, 4.97) * mm});
            skLineSegment(sketch, "E288", {"start": v(-63.93, 4.97) * mm, "end": v(-64.39, 4.93) * mm});
            skLineSegment(sketch, "E289", {"start": v(-64.39, 4.93) * mm, "end": v(-64.49, 4.93) * mm});
            skLineSegment(sketch, "E290", {"start": v(-64.49, 4.93) * mm, "end": v(-64.58, 4.92) * mm});
            skLineSegment(sketch, "E291", {"start": v(-64.58, 4.92) * mm, "end": v(-64.68, 4.9) * mm});
            skLineSegment(sketch, "E292", {"start": v(-64.68, 4.9) * mm, "end": v(-64.78, 4.9) * mm});
            skLineSegment(sketch, "E293", {"start": v(-64.78, 4.9) * mm, "end": v(-64.87, 4.87) * mm});
            skLineSegment(sketch, "E294", {"start": v(-64.87, 4.87) * mm, "end": v(-64.96, 4.84) * mm});
            skLineSegment(sketch, "E295", {"start": v(-64.96, 4.84) * mm, "end": v(-65.05, 4.81) * mm});
            skLineSegment(sketch, "E296", {"start": v(-65.05, 4.81) * mm, "end": v(-65.14, 4.78) * mm});
            skLineSegment(sketch, "E297", {"start": v(-65.14, 4.78) * mm, "end": v(-65.22, 4.74) * mm});
            skLineSegment(sketch, "E298", {"start": v(-65.22, 4.74) * mm, "end": v(-65.3, 4.7) * mm});
            skLineSegment(sketch, "E299", {"start": v(-65.3, 4.7) * mm, "end": v(-65.39, 4.65) * mm});
            skLineSegment(sketch, "E300", {"start": v(-65.39, 4.65) * mm, "end": v(-65.47, 4.6) * mm});
            skLineSegment(sketch, "E301", {"start": v(-65.47, 4.6) * mm, "end": v(-65.54, 4.55) * mm});
            skLineSegment(sketch, "E302", {"start": v(-65.54, 4.55) * mm, "end": v(-65.62, 4.5) * mm});
            skLineSegment(sketch, "E303", {"start": v(-65.62, 4.5) * mm, "end": v(-65.69, 4.43) * mm});
            skLineSegment(sketch, "E304", {"start": v(-65.69, 4.43) * mm, "end": v(-65.75, 4.37) * mm});
            skLineSegment(sketch, "E305", {"start": v(-65.75, 4.37) * mm, "end": v(-65.82, 4.3) * mm});
            skLineSegment(sketch, "E306", {"start": v(-65.82, 4.3) * mm, "end": v(-65.88, 4.23) * mm});
            skLineSegment(sketch, "E307", {"start": v(-65.88, 4.23) * mm, "end": v(-65.93, 4.16) * mm});
            skLineSegment(sketch, "E308", {"start": v(-65.93, 4.16) * mm, "end": v(-65.99, 4.08) * mm});
            skLineSegment(sketch, "E309", {"start": v(-65.99, 4.08) * mm, "end": v(-66.04, 4) * mm});
            skLineSegment(sketch, "E310", {"start": v(-66.04, 4) * mm, "end": v(-66.08, 3.92) * mm});
            skLineSegment(sketch, "E311", {"start": v(-66.08, 3.92) * mm, "end": v(-66.13, 3.84) * mm});
            skLineSegment(sketch, "E312", {"start": v(-66.13, 3.84) * mm, "end": v(-66.17, 3.75) * mm});
            skLineSegment(sketch, "E313", {"start": v(-66.17, 3.75) * mm, "end": v(-66.2, 3.66) * mm});
            skLineSegment(sketch, "E314", {"start": v(-66.2, 3.66) * mm, "end": v(-66.23, 3.57) * mm});
            skLineSegment(sketch, "E315", {"start": v(-66.23, 3.57) * mm, "end": v(-66.26, 3.48) * mm});
            skLineSegment(sketch, "E316", {"start": v(-66.26, 3.48) * mm, "end": v(-66.28, 3.39) * mm});
            skLineSegment(sketch, "E317", {"start": v(-66.28, 3.39) * mm, "end": v(-66.3, 3.3) * mm});
            skLineSegment(sketch, "E318", {"start": v(-66.3, 3.3) * mm, "end": v(-66.3, 3.2) * mm});
            skLineSegment(sketch, "E319", {"start": v(-66.3, 3.2) * mm, "end": v(-66.32, 3.1) * mm});
            skLineSegment(sketch, "E320", {"start": v(-66.32, 3.1) * mm, "end": v(-66.32, 3) * mm});
            skLineSegment(sketch, "E321", {"start": v(-66.32, 3) * mm, "end": v(-66.32, 2.9) * mm});
            skLineSegment(sketch, "E322", {"start": v(-66.32, 2.9) * mm, "end": v(-66.3, 2.8) * mm});
            skLineSegment(sketch, "E323", {"start": v(-66.3, 2.8) * mm, "end": v(-66.3, 2.7) * mm});
            skLineSegment(sketch, "E324", {"start": v(-66.3, 2.7) * mm, "end": v(-66.28, 2.61) * mm});
            skLineSegment(sketch, "E325", {"start": v(-66.28, 2.61) * mm, "end": v(-66.26, 2.52) * mm});
            skLineSegment(sketch, "E326", {"start": v(-66.26, 2.52) * mm, "end": v(-66.23, 2.43) * mm});
            skLineSegment(sketch, "E327", {"start": v(-66.23, 2.43) * mm, "end": v(-66.2, 2.34) * mm});
            skLineSegment(sketch, "E328", {"start": v(-66.2, 2.34) * mm, "end": v(-66.17, 2.25) * mm});
            skLineSegment(sketch, "E329", {"start": v(-66.17, 2.25) * mm, "end": v(-66.13, 2.16) * mm});
            skLineSegment(sketch, "E330", {"start": v(-66.13, 2.16) * mm, "end": v(-66.08, 2.08) * mm});
            skLineSegment(sketch, "E331", {"start": v(-66.08, 2.08) * mm, "end": v(-66.04, 2) * mm});
            skLineSegment(sketch, "E332", {"start": v(-66.04, 2) * mm, "end": v(-65.99, 1.92) * mm});
            skLineSegment(sketch, "E333", {"start": v(-65.99, 1.92) * mm, "end": v(-65.93, 1.85) * mm});
            skLineSegment(sketch, "E334", {"start": v(-65.93, 1.85) * mm, "end": v(-65.88, 1.77) * mm});
            skLineSegment(sketch, "E335", {"start": v(-65.88, 1.77) * mm, "end": v(-65.82, 1.7) * mm});
            skLineSegment(sketch, "E336", {"start": v(-65.82, 1.7) * mm, "end": v(-65.75, 1.64) * mm});
            skLineSegment(sketch, "E337", {"start": v(-65.75, 1.64) * mm, "end": v(-65.69, 1.57) * mm});
            skLineSegment(sketch, "E338", {"start": v(-65.69, 1.57) * mm, "end": v(-65.62, 1.51) * mm});
            skLineSegment(sketch, "E339", {"start": v(-65.62, 1.51) * mm, "end": v(-65.54, 1.45) * mm});
            skLineSegment(sketch, "E340", {"start": v(-65.54, 1.45) * mm, "end": v(-65.47, 1.4) * mm});
            skLineSegment(sketch, "E341", {"start": v(-65.47, 1.4) * mm, "end": v(-65.39, 1.35) * mm});
            skLineSegment(sketch, "E342", {"start": v(-65.39, 1.35) * mm, "end": v(-65.3, 1.3) * mm});
            skLineSegment(sketch, "E343", {"start": v(-65.3, 1.3) * mm, "end": v(-65.22, 1.26) * mm});
            skLineSegment(sketch, "E344", {"start": v(-65.22, 1.26) * mm, "end": v(-65.14, 1.22) * mm});
            skLineSegment(sketch, "E345", {"start": v(-65.14, 1.22) * mm, "end": v(-65.05, 1.19) * mm});
            skLineSegment(sketch, "E346", {"start": v(-65.05, 1.19) * mm, "end": v(-64.96, 1.16) * mm});
            skLineSegment(sketch, "E347", {"start": v(-64.96, 1.16) * mm, "end": v(-64.87, 1.13) * mm});
            skLineSegment(sketch, "E348", {"start": v(-64.87, 1.13) * mm, "end": v(-64.78, 1.1) * mm});
            skLineSegment(sketch, "E349", {"start": v(-64.78, 1.1) * mm, "end": v(-64.68, 1.1) * mm});
            skLineSegment(sketch, "E350", {"start": v(-64.68, 1.1) * mm, "end": v(-64.58, 1.08) * mm});
            skLineSegment(sketch, "E351", {"start": v(-64.58, 1.08) * mm, "end": v(-64.49, 1.07) * mm});
            skLineSegment(sketch, "E352", {"start": v(-64.49, 1.07) * mm, "end": v(-64.39, 1.07) * mm});
            skLineSegment(sketch, "E353", {"start": v(-64.39, 1.07) * mm, "end": v(-64.39, 1.07) * mm});
            skLineSegment(sketch, "E354", {"start": v(-64.39, 1.07) * mm, "end": v(-63.5, 0.98) * mm});
            skLineSegment(sketch, "E355", {"start": v(-63.5, 0.98) * mm, "end": v(-62.7, 0.86) * mm});
            skLineSegment(sketch, "E356", {"start": v(-62.7, 0.86) * mm, "end": v(-61.93, 0.73) * mm});
            skLineSegment(sketch, "E357", {"start": v(-61.93, 0.73) * mm, "end": v(-61.23, 0.57) * mm});
            skLineSegment(sketch, "E358", {"start": v(-61.23, 0.57) * mm, "end": v(-60.58, 0.4) * mm});
            skLineSegment(sketch, "E359", {"start": v(-60.58, 0.4) * mm, "end": v(-59.97, 0.2) * mm});
            skLineSegment(sketch, "E360", {"start": v(-59.97, 0.2) * mm, "end": v(-59.41, -0.03) * mm});
            skLineSegment(sketch, "E361", {"start": v(-59.41, -0.03) * mm, "end": v(-58.9, -0.27) * mm});
            skLineSegment(sketch, "E362", {"start": v(-58.9, -0.27) * mm, "end": v(-58.43, -0.53) * mm});
            skLineSegment(sketch, "E363", {"start": v(-58.43, -0.53) * mm, "end": v(-58, -0.8) * mm});
            skLineSegment(sketch, "E364", {"start": v(-58, -0.8) * mm, "end": v(-57.59, -1.1) * mm});
            skLineSegment(sketch, "E365", {"start": v(-57.59, -1.1) * mm, "end": v(-57.22, -1.42) * mm});
            skLineSegment(sketch, "E366", {"start": v(-57.22, -1.42) * mm, "end": v(-56.88, -1.75) * mm});
            skLineSegment(sketch, "E367", {"start": v(-56.88, -1.75) * mm, "end": v(-56.56, -2.1) * mm});
            skLineSegment(sketch, "E368", {"start": v(-56.56, -2.1) * mm, "end": v(-56.27, -2.47) * mm});
            skLineSegment(sketch, "E369", {"start": v(-56.27, -2.47) * mm, "end": v(-56, -2.86) * mm});
            skLineSegment(sketch, "E370", {"start": v(-56, -2.86) * mm, "end": v(-55.75, -3.26) * mm});
            skLineSegment(sketch, "E371", {"start": v(-55.75, -3.26) * mm, "end": v(-55.5, -3.68) * mm});
            skLineSegment(sketch, "E372", {"start": v(-55.5, -3.68) * mm, "end": v(-55.28, -4.1) * mm});
            skLineSegment(sketch, "E373", {"start": v(-55.28, -4.1) * mm, "end": v(-55.06, -4.56) * mm});
            skLineSegment(sketch, "E374", {"start": v(-55.06, -4.56) * mm, "end": v(-54.85, -5.02) * mm});
            skLineSegment(sketch, "E375", {"start": v(-54.85, -5.02) * mm, "end": v(-54.64, -5.5) * mm});
            skLineSegment(sketch, "E376", {"start": v(-54.64, -5.5) * mm, "end": v(-54.43, -5.99) * mm});
            skLineSegment(sketch, "E377", {"start": v(-54.43, -5.99) * mm, "end": v(-54.22, -6.5) * mm});
            skLineSegment(sketch, "E378", {"start": v(-54.22, -6.5) * mm, "end": v(-54, -7.01) * mm});
            skLineSegment(sketch, "E379", {"start": v(-54, -7.01) * mm, "end": v(-53.77, -7.55) * mm});
            skLineSegment(sketch, "E380", {"start": v(-53.77, -7.55) * mm, "end": v(-53.54, -8.1) * mm});
            skLineSegment(sketch, "E381", {"start": v(-53.54, -8.1) * mm, "end": v(-53.28, -8.65) * mm});
            skLineSegment(sketch, "E382", {"start": v(-53.28, -8.65) * mm, "end": v(-53.02, -9.21) * mm});
            skLineSegment(sketch, "E383", {"start": v(-53.02, -9.21) * mm, "end": v(-52.73, -9.8) * mm});
            skLineSegment(sketch, "E384", {"start": v(-52.73, -9.8) * mm, "end": v(-52.42, -10.38) * mm});
            skLineSegment(sketch, "E385", {"start": v(-52.42, -10.38) * mm, "end": v(-52.08, -10.99) * mm});
            skLineSegment(sketch, "E386", {"start": v(-52.08, -10.99) * mm, "end": v(-51.7, -11.63) * mm});
            skLineSegment(sketch, "E387", {"start": v(-51.7, -11.63) * mm, "end": v(-51.31, -12.27) * mm});
            skLineSegment(sketch, "E388", {"start": v(-51.31, -12.27) * mm, "end": v(-50.9, -12.9) * mm});
            skLineSegment(sketch, "E389", {"start": v(-50.9, -12.9) * mm, "end": v(-50.46, -13.5) * mm});
            skLineSegment(sketch, "E390", {"start": v(-50.46, -13.5) * mm, "end": v(-50, -14.1) * mm});
            skLineSegment(sketch, "E391", {"start": v(-50, -14.1) * mm, "end": v(-49.54, -14.67) * mm});
            skLineSegment(sketch, "E392", {"start": v(-49.54, -14.67) * mm, "end": v(-49.05, -15.23) * mm});
            skLineSegment(sketch, "E393", {"start": v(-49.05, -15.23) * mm, "end": v(-48.54, -15.77) * mm});
            skLineSegment(sketch, "E394", {"start": v(-48.54, -15.77) * mm, "end": v(-48.01, -16.3) * mm});
            skLineSegment(sketch, "E395", {"start": v(-48.01, -16.3) * mm, "end": v(-47.47, -16.81) * mm});
            skLineSegment(sketch, "E396", {"start": v(-47.47, -16.81) * mm, "end": v(-46.91, -17.3) * mm});
            skLineSegment(sketch, "E397", {"start": v(-46.91, -17.3) * mm, "end": v(-46.34, -17.78) * mm});
            skLineSegment(sketch, "E398", {"start": v(-46.34, -17.78) * mm, "end": v(-45.75, -18.23) * mm});
            skLineSegment(sketch, "E399", {"start": v(-45.75, -18.23) * mm, "end": v(-45.14, -18.67) * mm});
            skLineSegment(sketch, "E400", {"start": v(-45.14, -18.67) * mm, "end": v(-44.52, -19.09) * mm});
            skLineSegment(sketch, "E401", {"start": v(-44.52, -19.09) * mm, "end": v(-43.89, -19.48) * mm});
            skLineSegment(sketch, "E402", {"start": v(-43.89, -19.48) * mm, "end": v(-43.24, -19.86) * mm});
            skLineSegment(sketch, "E403", {"start": v(-43.24, -19.86) * mm, "end": v(-42.58, -20.22) * mm});
            skLineSegment(sketch, "E404", {"start": v(-42.58, -20.22) * mm, "end": v(-41.9, -20.55) * mm});
            skLineSegment(sketch, "E405", {"start": v(-41.9, -20.55) * mm, "end": v(-41.22, -20.86) * mm});
            skLineSegment(sketch, "E406", {"start": v(-41.22, -20.86) * mm, "end": v(-40.52, -21.15) * mm});
            skLineSegment(sketch, "E407", {"start": v(-40.52, -21.15) * mm, "end": v(-39.8, -21.42) * mm});
            skLineSegment(sketch, "E408", {"start": v(-39.8, -21.42) * mm, "end": v(-39.09, -21.66) * mm});
            skLineSegment(sketch, "E409", {"start": v(-39.09, -21.66) * mm, "end": v(-38.36, -21.88) * mm});
            skLineSegment(sketch, "E410", {"start": v(-38.36, -21.88) * mm, "end": v(-37.62, -22.08) * mm});
            skLineSegment(sketch, "E411", {"start": v(-37.62, -22.08) * mm, "end": v(-36.86, -22.25) * mm});
            skLineSegment(sketch, "E412", {"start": v(-36.86, -22.25) * mm, "end": v(-36.1, -22.4) * mm});
            skLineSegment(sketch, "E413", {"start": v(-36.1, -22.4) * mm, "end": v(-35.34, -22.52) * mm});
            skLineSegment(sketch, "E414", {"start": v(-35.34, -22.52) * mm, "end": v(-34.56, -22.61) * mm});
            skLineSegment(sketch, "E415", {"start": v(-34.56, -22.61) * mm, "end": v(-33.78, -22.68) * mm});
            skLineSegment(sketch, "E416", {"start": v(-33.78, -22.68) * mm, "end": v(-32.98, -22.72) * mm});
            skLineSegment(sketch, "E417", {"start": v(-32.98, -22.72) * mm, "end": v(-32.19, -22.73) * mm});
            skLineSegment(sketch, "E418", {"start": v(-32.19, -22.73) * mm, "end": v(-31.32, -22.72) * mm});
            skLineSegment(sketch, "E419", {"start": v(-31.32, -22.72) * mm, "end": v(-30.46, -22.67) * mm});
            skLineSegment(sketch, "E420", {"start": v(-30.46, -22.67) * mm, "end": v(-29.6, -22.59) * mm});
            skLineSegment(sketch, "E421", {"start": v(-29.6, -22.59) * mm, "end": v(-28.76, -22.48) * mm});
            skLineSegment(sketch, "E422", {"start": v(-28.76, -22.48) * mm, "end": v(-27.93, -22.33) * mm});
            skLineSegment(sketch, "E423", {"start": v(-27.93, -22.33) * mm, "end": v(-27.11, -22.16) * mm});
            skLineSegment(sketch, "E424", {"start": v(-27.11, -22.16) * mm, "end": v(-26.3, -21.96) * mm});
            skLineSegment(sketch, "E425", {"start": v(-26.3, -21.96) * mm, "end": v(-25.5, -21.73) * mm});
            skLineSegment(sketch, "E426", {"start": v(-25.5, -21.73) * mm, "end": v(-24.71, -21.47) * mm});
            skLineSegment(sketch, "E427", {"start": v(-24.71, -21.47) * mm, "end": v(-23.94, -21.19) * mm});
            skLineSegment(sketch, "E428", {"start": v(-23.94, -21.19) * mm, "end": v(-23.18, -20.87) * mm});
            skLineSegment(sketch, "E429", {"start": v(-23.18, -20.87) * mm, "end": v(-22.43, -20.53) * mm});
            skLineSegment(sketch, "E430", {"start": v(-22.43, -20.53) * mm, "end": v(-21.7, -20.17) * mm});
            skLineSegment(sketch, "E431", {"start": v(-21.7, -20.17) * mm, "end": v(-20.99, -19.78) * mm});
            skLineSegment(sketch, "E432", {"start": v(-20.99, -19.78) * mm, "end": v(-20.29, -19.36) * mm});
            skLineSegment(sketch, "E433", {"start": v(-20.29, -19.36) * mm, "end": v(-19.6, -18.92) * mm});
            skLineSegment(sketch, "E434", {"start": v(-19.6, -18.92) * mm, "end": v(-18.93, -18.46) * mm});
            skLineSegment(sketch, "E435", {"start": v(-18.93, -18.46) * mm, "end": v(-18.28, -17.97) * mm});
            skLineSegment(sketch, "E436", {"start": v(-18.28, -17.97) * mm, "end": v(-17.65, -17.47) * mm});
            skLineSegment(sketch, "E437", {"start": v(-17.65, -17.47) * mm, "end": v(-17.04, -16.94) * mm});
            skLineSegment(sketch, "E438", {"start": v(-17.04, -16.94) * mm, "end": v(-16.45, -16.39) * mm});
            skLineSegment(sketch, "E439", {"start": v(-16.45, -16.39) * mm, "end": v(-15.87, -15.81) * mm});
            skLineSegment(sketch, "E440", {"start": v(-15.87, -15.81) * mm, "end": v(-15.32, -15.22) * mm});
            skLineSegment(sketch, "E441", {"start": v(-15.32, -15.22) * mm, "end": v(-14.79, -14.61) * mm});
            skLineSegment(sketch, "E442", {"start": v(-14.79, -14.61) * mm, "end": v(-14.28, -13.98) * mm});
            skLineSegment(sketch, "E443", {"start": v(-14.28, -13.98) * mm, "end": v(-13.79, -13.33) * mm});
            skLineSegment(sketch, "E444", {"start": v(-13.79, -13.33) * mm, "end": v(-13.32, -12.67) * mm});
            skLineSegment(sketch, "E445", {"start": v(-13.32, -12.67) * mm, "end": v(-12.88, -11.99) * mm});
            skLineSegment(sketch, "E446", {"start": v(-12.88, -11.99) * mm, "end": v(-12.46, -11.29) * mm});
            skLineSegment(sketch, "E447", {"start": v(-12.46, -11.29) * mm, "end": v(-12.07, -10.57) * mm});
            skLineSegment(sketch, "E448", {"start": v(-12.07, -10.57) * mm, "end": v(-11.7, -9.84) * mm});
            skLineSegment(sketch, "E449", {"start": v(-11.7, -9.84) * mm, "end": v(-11.36, -9.1) * mm});
            skLineSegment(sketch, "E450", {"start": v(-11.36, -9.1) * mm, "end": v(-11.32, -9.02) * mm});
            skLineSegment(sketch, "E451", {"start": v(-11.32, -9.02) * mm, "end": v(-11.29, -8.94) * mm});
            skLineSegment(sketch, "E452", {"start": v(-11.29, -8.94) * mm, "end": v(-11.25, -8.86) * mm});
            skLineSegment(sketch, "E453", {"start": v(-11.25, -8.86) * mm, "end": v(-11.22, -8.78) * mm});
            skLineSegment(sketch, "E454", {"start": v(-11.22, -8.78) * mm, "end": v(-11.19, -8.7) * mm});
            skLineSegment(sketch, "E455", {"start": v(-11.19, -8.7) * mm, "end": v(-11.15, -8.62) * mm});
            skLineSegment(sketch, "E456", {"start": v(-11.15, -8.62) * mm, "end": v(-11.12, -8.53) * mm});
            skLineSegment(sketch, "E457", {"start": v(-11.12, -8.53) * mm, "end": v(-11.09, -8.45) * mm});
            skLineSegment(sketch, "E458", {"start": v(-11.09, -8.45) * mm, "end": v(-11.05, -8.37) * mm});
            skLineSegment(sketch, "E459", {"start": v(-11.05, -8.37) * mm, "end": v(-11.02, -8.29) * mm});
            skLineSegment(sketch, "E460", {"start": v(-11.02, -8.29) * mm, "end": v(-10.99, -8.2) * mm});
            skLineSegment(sketch, "E461", {"start": v(-10.99, -8.2) * mm, "end": v(-10.96, -8.12) * mm});
            skLineSegment(sketch, "E462", {"start": v(-10.96, -8.12) * mm, "end": v(-10.93, -8.04) * mm});
            skLineSegment(sketch, "E463", {"start": v(-10.93, -8.04) * mm, "end": v(-10.9, -7.95) * mm});
            skLineSegment(sketch, "E464", {"start": v(-10.9, -7.95) * mm, "end": v(-10.86, -7.87) * mm});
            skLineSegment(sketch, "E465", {"start": v(-10.86, -7.87) * mm, "end": v(-10.83, -7.79) * mm});
            skLineSegment(sketch, "E466", {"start": v(-10.83, -7.79) * mm, "end": v(-10.8, -7.7) * mm});
            skLineSegment(sketch, "E467", {"start": v(-10.8, -7.7) * mm, "end": v(-10.77, -7.62) * mm});
            skLineSegment(sketch, "E468", {"start": v(-10.77, -7.62) * mm, "end": v(-10.74, -7.53) * mm});
            skLineSegment(sketch, "E469", {"start": v(-10.74, -7.53) * mm, "end": v(-10.71, -7.45) * mm});
            skLineSegment(sketch, "E470", {"start": v(-10.71, -7.45) * mm, "end": v(-10.68, -7.37) * mm});
            skLineSegment(sketch, "E471", {"start": v(-10.68, -7.37) * mm, "end": v(-10.65, -7.28) * mm});
            skLineSegment(sketch, "E472", {"start": v(-10.65, -7.28) * mm, "end": v(-10.63, -7.2) * mm});
            skLineSegment(sketch, "E473", {"start": v(-10.63, -7.2) * mm, "end": v(-10.6, -7.11) * mm});
            skLineSegment(sketch, "E474", {"start": v(-10.6, -7.11) * mm, "end": v(-10.57, -7.03) * mm});
            skLineSegment(sketch, "E475", {"start": v(-10.57, -7.03) * mm, "end": v(-10.54, -6.94) * mm});
            skLineSegment(sketch, "E476", {"start": v(-10.54, -6.94) * mm, "end": v(-10.51, -6.86) * mm});
            skLineSegment(sketch, "E477", {"start": v(-10.51, -6.86) * mm, "end": v(-10.49, -6.78) * mm});
            skLineSegment(sketch, "E478", {"start": v(-10.49, -6.78) * mm, "end": v(-10.46, -6.7) * mm});
            skLineSegment(sketch, "E479", {"start": v(-10.46, -6.7) * mm, "end": v(-10.44, -6.6) * mm});
            skLineSegment(sketch, "E480", {"start": v(-10.44, -6.6) * mm, "end": v(-10.41, -6.52) * mm});
            skLineSegment(sketch, "E481", {"start": v(-10.41, -6.52) * mm, "end": v(-10.39, -6.44) * mm});
            skLineSegment(sketch, "E482", {"start": v(-10.39, -6.44) * mm, "end": v(-10.22, -5.95) * mm});
            skLineSegment(sketch, "E483", {"start": v(-10.22, -5.95) * mm, "end": v(-10.05, -5.47) * mm});
            skLineSegment(sketch, "E484", {"start": v(-10.05, -5.47) * mm, "end": v(-9.89, -4.99) * mm});
            skLineSegment(sketch, "E485", {"start": v(-9.89, -4.99) * mm, "end": v(-9.72, -4.52) * mm});
            skLineSegment(sketch, "E486", {"start": v(-9.72, -4.52) * mm, "end": v(-9.56, -4.06) * mm});
            skLineSegment(sketch, "E487", {"start": v(-9.56, -4.06) * mm, "end": v(-9.39, -3.6) * mm});
            skLineSegment(sketch, "E488", {"start": v(-9.39, -3.6) * mm, "end": v(-9.21, -3.15) * mm});
            skLineSegment(sketch, "E489", {"start": v(-9.21, -3.15) * mm, "end": v(-9.03, -2.72) * mm});
            skLineSegment(sketch, "E490", {"start": v(-9.03, -2.72) * mm, "end": v(-8.84, -2.29) * mm});
            skLineSegment(sketch, "E491", {"start": v(-8.84, -2.29) * mm, "end": v(-8.65, -1.87) * mm});
            skLineSegment(sketch, "E492", {"start": v(-8.65, -1.87) * mm, "end": v(-8.45, -1.47) * mm});
            skLineSegment(sketch, "E493", {"start": v(-8.45, -1.47) * mm, "end": v(-8.23, -1.07) * mm});
            skLineSegment(sketch, "E494", {"start": v(-8.23, -1.07) * mm, "end": v(-8.01, -0.7) * mm});
            skLineSegment(sketch, "E495", {"start": v(-8.01, -0.7) * mm, "end": v(-7.77, -0.32) * mm});
            skLineSegment(sketch, "E496", {"start": v(-7.77, -0.32) * mm, "end": v(-7.52, 0.03) * mm});
            skLineSegment(sketch, "E497", {"start": v(-7.52, 0.03) * mm, "end": v(-7.26, 0.37) * mm});
            skLineSegment(sketch, "E498", {"start": v(-7.26, 0.37) * mm, "end": v(-6.97, 0.7) * mm});
            skLineSegment(sketch, "E499", {"start": v(-6.97, 0.7) * mm, "end": v(-6.68, 1) * mm});
            skLineSegment(sketch, "E500", {"start": v(-6.68, 1) * mm, "end": v(-6.36, 1.3) * mm});
            skLineSegment(sketch, "E501", {"start": v(-6.36, 1.3) * mm, "end": v(-6.02, 1.57) * mm});
            skLineSegment(sketch, "E502", {"start": v(-6.02, 1.57) * mm, "end": v(-5.66, 1.82) * mm});
            skLineSegment(sketch, "E503", {"start": v(-5.66, 1.82) * mm, "end": v(-5.28, 2.06) * mm});
            skLineSegment(sketch, "E504", {"start": v(-5.28, 2.06) * mm, "end": v(-4.88, 2.28) * mm});
            skLineSegment(sketch, "E505", {"start": v(-4.88, 2.28) * mm, "end": v(-4.45, 2.47) * mm});
            skLineSegment(sketch, "E506", {"start": v(-4.45, 2.47) * mm, "end": v(-4, 2.65) * mm});
            skLineSegment(sketch, "E507", {"start": v(-4, 2.65) * mm, "end": v(-3.52, 2.8) * mm});
            skLineSegment(sketch, "E508", {"start": v(-3.52, 2.8) * mm, "end": v(-3, 2.94) * mm});
            skLineSegment(sketch, "E509", {"start": v(-3, 2.94) * mm, "end": v(-2.47, 3.05) * mm});
            skLineSegment(sketch, "E510", {"start": v(-2.47, 3.05) * mm, "end": v(-1.9, 3.14) * mm});
            skLineSegment(sketch, "E511", {"start": v(-1.9, 3.14) * mm, "end": v(-1.3, 3.2) * mm});
            skLineSegment(sketch, "E512", {"start": v(-1.3, 3.2) * mm, "end": v(-0.67, 3.24) * mm});
            skLineSegment(sketch, "E513", {"start": v(-0.67, 3.24) * mm, "end": v(0, 3.25) * mm});
            skLineSegment(sketch, "E514", {"start": v(0, 3.25) * mm, "end": v(0.67, 3.24) * mm});
            skLineSegment(sketch, "E515", {"start": v(0.67, 3.24) * mm, "end": v(1.3, 3.2) * mm});
            skLineSegment(sketch, "E516", {"start": v(1.3, 3.2) * mm, "end": v(1.9, 3.14) * mm});
            skLineSegment(sketch, "E517", {"start": v(1.9, 3.14) * mm, "end": v(2.47, 3.05) * mm});
            skLineSegment(sketch, "E518", {"start": v(2.47, 3.05) * mm, "end": v(3, 2.94) * mm});
            skLineSegment(sketch, "E519", {"start": v(3, 2.94) * mm, "end": v(3.52, 2.8) * mm});
            skLineSegment(sketch, "E520", {"start": v(3.52, 2.8) * mm, "end": v(4, 2.65) * mm});
            skLineSegment(sketch, "E521", {"start": v(4, 2.65) * mm, "end": v(4.45, 2.47) * mm});
            skLineSegment(sketch, "E522", {"start": v(4.45, 2.47) * mm, "end": v(4.88, 2.28) * mm});
            skLineSegment(sketch, "E523", {"start": v(4.88, 2.28) * mm, "end": v(5.28, 2.06) * mm});
            skLineSegment(sketch, "E524", {"start": v(5.28, 2.06) * mm, "end": v(5.66, 1.82) * mm});
            skLineSegment(sketch, "E525", {"start": v(5.66, 1.82) * mm, "end": v(6.02, 1.57) * mm});
            skLineSegment(sketch, "E526", {"start": v(6.02, 1.57) * mm, "end": v(6.36, 1.3) * mm});
            skLineSegment(sketch, "E527", {"start": v(6.36, 1.3) * mm, "end": v(6.68, 1) * mm});
            skLineSegment(sketch, "E528", {"start": v(6.68, 1) * mm, "end": v(6.97, 0.7) * mm});
            skLineSegment(sketch, "E529", {"start": v(6.97, 0.7) * mm, "end": v(7.26, 0.37) * mm});
            skLineSegment(sketch, "E530", {"start": v(7.26, 0.37) * mm, "end": v(7.52, 0.03) * mm});
            skLineSegment(sketch, "E531", {"start": v(7.52, 0.03) * mm, "end": v(7.77, -0.32) * mm});
            skLineSegment(sketch, "E532", {"start": v(7.77, -0.32) * mm, "end": v(8.01, -0.7) * mm});
            skLineSegment(sketch, "E533", {"start": v(8.01, -0.7) * mm, "end": v(8.23, -1.07) * mm});
            skLineSegment(sketch, "E534", {"start": v(8.23, -1.07) * mm, "end": v(8.45, -1.47) * mm});
            skLineSegment(sketch, "E535", {"start": v(8.45, -1.47) * mm, "end": v(8.65, -1.87) * mm});
            skLineSegment(sketch, "E536", {"start": v(8.65, -1.87) * mm, "end": v(8.84, -2.29) * mm});
            skLineSegment(sketch, "E537", {"start": v(8.84, -2.29) * mm, "end": v(9.03, -2.72) * mm});
            skLineSegment(sketch, "E538", {"start": v(9.03, -2.72) * mm, "end": v(9.21, -3.15) * mm});
            skLineSegment(sketch, "E539", {"start": v(9.21, -3.15) * mm, "end": v(9.39, -3.6) * mm});
            skLineSegment(sketch, "E540", {"start": v(9.39, -3.6) * mm, "end": v(9.56, -4.06) * mm});
            skLineSegment(sketch, "E541", {"start": v(9.56, -4.06) * mm, "end": v(9.72, -4.52) * mm});
            skLineSegment(sketch, "E542", {"start": v(9.72, -4.52) * mm, "end": v(9.89, -4.99) * mm});
            skLineSegment(sketch, "E543", {"start": v(9.89, -4.99) * mm, "end": v(10.05, -5.47) * mm});
            skLineSegment(sketch, "E544", {"start": v(10.05, -5.47) * mm, "end": v(10.22, -5.95) * mm});
            skLineSegment(sketch, "E545", {"start": v(10.22, -5.95) * mm, "end": v(10.39, -6.44) * mm});
            skLineSegment(sketch, "E546", {"start": v(10.39, -6.44) * mm, "end": v(10.41, -6.52) * mm});
            skLineSegment(sketch, "E547", {"start": v(10.41, -6.52) * mm, "end": v(10.44, -6.6) * mm});
            skLineSegment(sketch, "E548", {"start": v(10.44, -6.6) * mm, "end": v(10.46, -6.7) * mm});
            skLineSegment(sketch, "E549", {"start": v(10.46, -6.7) * mm, "end": v(10.49, -6.78) * mm});
            skLineSegment(sketch, "E550", {"start": v(10.49, -6.78) * mm, "end": v(10.51, -6.86) * mm});
            skLineSegment(sketch, "E551", {"start": v(10.51, -6.86) * mm, "end": v(10.54, -6.94) * mm});
            skLineSegment(sketch, "E552", {"start": v(10.54, -6.94) * mm, "end": v(10.57, -7.03) * mm});
            skLineSegment(sketch, "E553", {"start": v(10.57, -7.03) * mm, "end": v(10.6, -7.11) * mm});
            skLineSegment(sketch, "E554", {"start": v(10.6, -7.11) * mm, "end": v(10.63, -7.2) * mm});
            skLineSegment(sketch, "E555", {"start": v(10.63, -7.2) * mm, "end": v(10.65, -7.28) * mm});
            skLineSegment(sketch, "E556", {"start": v(10.65, -7.28) * mm, "end": v(10.68, -7.37) * mm});
            skLineSegment(sketch, "E557", {"start": v(10.68, -7.37) * mm, "end": v(10.71, -7.45) * mm});
            skLineSegment(sketch, "E558", {"start": v(10.71, -7.45) * mm, "end": v(10.74, -7.53) * mm});
            skLineSegment(sketch, "E559", {"start": v(10.74, -7.53) * mm, "end": v(10.77, -7.62) * mm});
            skLineSegment(sketch, "E560", {"start": v(10.77, -7.62) * mm, "end": v(10.8, -7.7) * mm});
            skLineSegment(sketch, "E561", {"start": v(10.8, -7.7) * mm, "end": v(10.83, -7.79) * mm});
            skLineSegment(sketch, "E562", {"start": v(10.83, -7.79) * mm, "end": v(10.86, -7.87) * mm});
            skLineSegment(sketch, "E563", {"start": v(10.86, -7.87) * mm, "end": v(10.9, -7.95) * mm});
            skLineSegment(sketch, "E564", {"start": v(10.9, -7.95) * mm, "end": v(10.93, -8.04) * mm});
            skLineSegment(sketch, "E565", {"start": v(10.93, -8.04) * mm, "end": v(10.96, -8.12) * mm});
            skLineSegment(sketch, "E566", {"start": v(10.96, -8.12) * mm, "end": v(10.99, -8.2) * mm});
            skLineSegment(sketch, "E567", {"start": v(10.99, -8.2) * mm, "end": v(11.02, -8.29) * mm});
            skLineSegment(sketch, "E568", {"start": v(11.02, -8.29) * mm, "end": v(11.05, -8.37) * mm});
            skLineSegment(sketch, "E569", {"start": v(11.05, -8.37) * mm, "end": v(11.09, -8.45) * mm});
            skLineSegment(sketch, "E570", {"start": v(11.09, -8.45) * mm, "end": v(11.12, -8.53) * mm});
            skLineSegment(sketch, "E571", {"start": v(11.12, -8.53) * mm, "end": v(11.15, -8.62) * mm});
            skLineSegment(sketch, "E572", {"start": v(11.15, -8.62) * mm, "end": v(11.19, -8.7) * mm});
            skLineSegment(sketch, "E573", {"start": v(11.19, -8.7) * mm, "end": v(11.22, -8.78) * mm});
            skLineSegment(sketch, "E574", {"start": v(11.22, -8.78) * mm, "end": v(11.25, -8.86) * mm});
            skLineSegment(sketch, "E575", {"start": v(11.25, -8.86) * mm, "end": v(11.29, -8.94) * mm});
            skLineSegment(sketch, "E576", {"start": v(11.29, -8.94) * mm, "end": v(11.32, -9.02) * mm});
            skLineSegment(sketch, "E577", {"start": v(11.32, -9.02) * mm, "end": v(11.36, -9.1) * mm});
            skLineSegment(sketch, "E578", {"start": v(11.36, -9.1) * mm, "end": v(11.7, -9.84) * mm});
            skLineSegment(sketch, "E579", {"start": v(11.7, -9.84) * mm, "end": v(12.07, -10.57) * mm});
            skLineSegment(sketch, "E580", {"start": v(12.07, -10.57) * mm, "end": v(12.46, -11.29) * mm});
            skLineSegment(sketch, "E581", {"start": v(12.46, -11.29) * mm, "end": v(12.88, -11.99) * mm});
            skLineSegment(sketch, "E582", {"start": v(12.88, -11.99) * mm, "end": v(13.32, -12.67) * mm});
            skLineSegment(sketch, "E583", {"start": v(13.32, -12.67) * mm, "end": v(13.79, -13.33) * mm});
            skLineSegment(sketch, "E584", {"start": v(13.79, -13.33) * mm, "end": v(14.28, -13.98) * mm});
            skLineSegment(sketch, "E585", {"start": v(14.28, -13.98) * mm, "end": v(14.79, -14.61) * mm});
            skLineSegment(sketch, "E586", {"start": v(14.79, -14.61) * mm, "end": v(15.32, -15.22) * mm});
            skLineSegment(sketch, "E587", {"start": v(15.32, -15.22) * mm, "end": v(15.87, -15.81) * mm});
            skLineSegment(sketch, "E588", {"start": v(15.87, -15.81) * mm, "end": v(16.45, -16.39) * mm});
            skLineSegment(sketch, "E589", {"start": v(16.45, -16.39) * mm, "end": v(17.04, -16.94) * mm});
            skLineSegment(sketch, "E590", {"start": v(17.04, -16.94) * mm, "end": v(17.65, -17.47) * mm});
            skLineSegment(sketch, "E591", {"start": v(17.65, -17.47) * mm, "end": v(18.28, -17.97) * mm});
            skLineSegment(sketch, "E592", {"start": v(18.28, -17.97) * mm, "end": v(18.93, -18.46) * mm});
            skLineSegment(sketch, "E593", {"start": v(18.93, -18.46) * mm, "end": v(19.6, -18.92) * mm});
            skLineSegment(sketch, "E594", {"start": v(19.6, -18.92) * mm, "end": v(20.29, -19.36) * mm});
            skLineSegment(sketch, "E595", {"start": v(20.29, -19.36) * mm, "end": v(20.99, -19.78) * mm});
            skLineSegment(sketch, "E596", {"start": v(20.99, -19.78) * mm, "end": v(21.7, -20.17) * mm});
            skLineSegment(sketch, "E597", {"start": v(21.7, -20.17) * mm, "end": v(22.43, -20.53) * mm});
            skLineSegment(sketch, "E598", {"start": v(22.43, -20.53) * mm, "end": v(23.18, -20.87) * mm});
            skLineSegment(sketch, "E599", {"start": v(23.18, -20.87) * mm, "end": v(23.94, -21.19) * mm});
            skLineSegment(sketch, "E600", {"start": v(23.94, -21.19) * mm, "end": v(24.71, -21.47) * mm});
            skLineSegment(sketch, "E601", {"start": v(24.71, -21.47) * mm, "end": v(25.5, -21.73) * mm});
            skLineSegment(sketch, "E602", {"start": v(25.5, -21.73) * mm, "end": v(26.3, -21.96) * mm});
            skLineSegment(sketch, "E603", {"start": v(26.3, -21.96) * mm, "end": v(27.11, -22.16) * mm});
            skLineSegment(sketch, "E604", {"start": v(27.11, -22.16) * mm, "end": v(27.93, -22.33) * mm});
            skLineSegment(sketch, "E605", {"start": v(27.93, -22.33) * mm, "end": v(28.76, -22.48) * mm});
            skLineSegment(sketch, "E606", {"start": v(28.76, -22.48) * mm, "end": v(29.6, -22.59) * mm});
            skLineSegment(sketch, "E607", {"start": v(29.6, -22.59) * mm, "end": v(30.46, -22.67) * mm});
            skLineSegment(sketch, "E608", {"start": v(30.46, -22.67) * mm, "end": v(31.32, -22.72) * mm});
            skLineSegment(sketch, "E609", {"start": v(31.32, -22.72) * mm, "end": v(32.19, -22.73) * mm});
            skLineSegment(sketch, "E610", {"start": v(32.19, -22.73) * mm, "end": v(32.98, -22.72) * mm});
            skLineSegment(sketch, "E611", {"start": v(32.98, -22.72) * mm, "end": v(33.78, -22.68) * mm});
            skLineSegment(sketch, "E612", {"start": v(33.78, -22.68) * mm, "end": v(34.56, -22.61) * mm});
            skLineSegment(sketch, "E613", {"start": v(34.56, -22.61) * mm, "end": v(35.34, -22.52) * mm});
            skLineSegment(sketch, "E614", {"start": v(35.34, -22.52) * mm, "end": v(36.1, -22.4) * mm});
            skLineSegment(sketch, "E615", {"start": v(36.1, -22.4) * mm, "end": v(36.86, -22.25) * mm});
            skLineSegment(sketch, "E616", {"start": v(36.86, -22.25) * mm, "end": v(37.62, -22.08) * mm});
            skLineSegment(sketch, "E617", {"start": v(37.62, -22.08) * mm, "end": v(38.36, -21.88) * mm});
            skLineSegment(sketch, "E618", {"start": v(38.36, -21.88) * mm, "end": v(39.09, -21.66) * mm});
            skLineSegment(sketch, "E619", {"start": v(39.09, -21.66) * mm, "end": v(39.8, -21.42) * mm});
            skLineSegment(sketch, "E620", {"start": v(39.8, -21.42) * mm, "end": v(40.52, -21.15) * mm});
            skLineSegment(sketch, "E621", {"start": v(40.52, -21.15) * mm, "end": v(41.22, -20.86) * mm});
            skLineSegment(sketch, "E622", {"start": v(41.22, -20.86) * mm, "end": v(41.9, -20.55) * mm});
            skLineSegment(sketch, "E623", {"start": v(41.9, -20.55) * mm, "end": v(42.58, -20.22) * mm});
            skLineSegment(sketch, "E624", {"start": v(42.58, -20.22) * mm, "end": v(43.24, -19.86) * mm});
            skLineSegment(sketch, "E625", {"start": v(43.24, -19.86) * mm, "end": v(43.88, -19.49) * mm});
            skLineSegment(sketch, "E626", {"start": v(43.88, -19.49) * mm, "end": v(44.52, -19.1) * mm});
            skLineSegment(sketch, "E627", {"start": v(44.52, -19.1) * mm, "end": v(45.14, -18.68) * mm});
            skLineSegment(sketch, "E628", {"start": v(45.14, -18.68) * mm, "end": v(45.74, -18.24) * mm});
            skLineSegment(sketch, "E629", {"start": v(45.74, -18.24) * mm, "end": v(46.33, -17.78) * mm});
            skLineSegment(sketch, "E630", {"start": v(46.33, -17.78) * mm, "end": v(46.9, -17.3) * mm});
            skLineSegment(sketch, "E631", {"start": v(46.9, -17.3) * mm, "end": v(47.47, -16.82) * mm});
            skLineSegment(sketch, "E632", {"start": v(47.47, -16.82) * mm, "end": v(48.01, -16.3) * mm});
            skLineSegment(sketch, "E633", {"start": v(48.01, -16.3) * mm, "end": v(48.54, -15.78) * mm});
            skLineSegment(sketch, "E634", {"start": v(48.54, -15.78) * mm, "end": v(49.04, -15.24) * mm});
            skLineSegment(sketch, "E635", {"start": v(49.04, -15.24) * mm, "end": v(49.54, -14.68) * mm});
            skLineSegment(sketch, "E636", {"start": v(49.54, -14.68) * mm, "end": v(50, -14.1) * mm});
            skLineSegment(sketch, "E637", {"start": v(50, -14.1) * mm, "end": v(50.46, -13.5) * mm});
            skLineSegment(sketch, "E638", {"start": v(50.46, -13.5) * mm, "end": v(50.9, -12.9) * mm});
            skLineSegment(sketch, "E639", {"start": v(50.9, -12.9) * mm, "end": v(51.31, -12.28) * mm});
            skLineSegment(sketch, "E640", {"start": v(51.31, -12.28) * mm, "end": v(51.7, -11.64) * mm});
            skLineSegment(sketch, "E641", {"start": v(51.7, -11.64) * mm, "end": v(52.08, -11) * mm});
            skLineSegment(sketch, "E642", {"start": v(52.08, -11) * mm, "end": v(52.42, -10.4) * mm});
            skLineSegment(sketch, "E643", {"start": v(52.42, -10.4) * mm, "end": v(52.73, -9.8) * mm});
            skLineSegment(sketch, "E644", {"start": v(52.73, -9.8) * mm, "end": v(53.02, -9.22) * mm});
            skLineSegment(sketch, "E645", {"start": v(53.02, -9.22) * mm, "end": v(53.28, -8.65) * mm});
            skLineSegment(sketch, "E646", {"start": v(53.28, -8.65) * mm, "end": v(53.54, -8.1) * mm});
            skLineSegment(sketch, "E647", {"start": v(53.54, -8.1) * mm, "end": v(53.77, -7.55) * mm});
            skLineSegment(sketch, "E648", {"start": v(53.77, -7.55) * mm, "end": v(54, -7.02) * mm});
            skLineSegment(sketch, "E649", {"start": v(54, -7.02) * mm, "end": v(54.22, -6.5) * mm});
            skLineSegment(sketch, "E650", {"start": v(54.22, -6.5) * mm, "end": v(54.43, -6) * mm});
            skLineSegment(sketch, "E651", {"start": v(54.43, -6) * mm, "end": v(54.64, -5.5) * mm});
            skLineSegment(sketch, "E652", {"start": v(54.64, -5.5) * mm, "end": v(54.85, -5.03) * mm});
            skLineSegment(sketch, "E653", {"start": v(54.85, -5.03) * mm, "end": v(55.06, -4.56) * mm});
            skLineSegment(sketch, "E654", {"start": v(55.06, -4.56) * mm, "end": v(55.28, -4.11) * mm});
            skLineSegment(sketch, "E655", {"start": v(55.28, -4.11) * mm, "end": v(55.5, -3.68) * mm});
            skLineSegment(sketch, "E656", {"start": v(55.5, -3.68) * mm, "end": v(55.75, -3.26) * mm});
            skLineSegment(sketch, "E657", {"start": v(55.75, -3.26) * mm, "end": v(56, -2.86) * mm});
            skLineSegment(sketch, "E658", {"start": v(56, -2.86) * mm, "end": v(56.27, -2.48) * mm});
            skLineSegment(sketch, "E659", {"start": v(56.27, -2.48) * mm, "end": v(56.56, -2.1) * mm});
            skLineSegment(sketch, "E660", {"start": v(56.56, -2.1) * mm, "end": v(56.88, -1.75) * mm});
            skLineSegment(sketch, "E661", {"start": v(56.88, -1.75) * mm, "end": v(57.22, -1.42) * mm});
            skLineSegment(sketch, "E662", {"start": v(57.22, -1.42) * mm, "end": v(57.59, -1.1) * mm});
            skLineSegment(sketch, "E663", {"start": v(57.59, -1.1) * mm, "end": v(58, -0.8) * mm});
            skLineSegment(sketch, "E664", {"start": v(58, -0.8) * mm, "end": v(58.43, -0.53) * mm});
            skLineSegment(sketch, "E665", {"start": v(58.43, -0.53) * mm, "end": v(58.9, -0.27) * mm});
            skLineSegment(sketch, "E666", {"start": v(58.9, -0.27) * mm, "end": v(59.41, -0.03) * mm});
            skLineSegment(sketch, "E667", {"start": v(59.41, -0.03) * mm, "end": v(59.97, 0.2) * mm});
            skLineSegment(sketch, "E668", {"start": v(59.97, 0.2) * mm, "end": v(60.58, 0.4) * mm});
            skLineSegment(sketch, "E669", {"start": v(60.58, 0.4) * mm, "end": v(61.23, 0.57) * mm});
            skLineSegment(sketch, "E670", {"start": v(61.23, 0.57) * mm, "end": v(61.93, 0.73) * mm});
            skLineSegment(sketch, "E671", {"start": v(61.93, 0.73) * mm, "end": v(62.7, 0.86) * mm});
            skLineSegment(sketch, "E672", {"start": v(62.7, 0.86) * mm, "end": v(63.5, 0.98) * mm});
            skLineSegment(sketch, "E673", {"start": v(63.5, 0.98) * mm, "end": v(64.39, 1.07) * mm});
            skLineSegment(sketch, "E674", {"start": v(64.39, 1.07) * mm, "end": v(64.49, 1.07) * mm});
            skLineSegment(sketch, "E675", {"start": v(64.49, 1.07) * mm, "end": v(64.58, 1.08) * mm});
            skLineSegment(sketch, "E676", {"start": v(64.58, 1.08) * mm, "end": v(64.68, 1.1) * mm});
            skLineSegment(sketch, "E677", {"start": v(64.68, 1.1) * mm, "end": v(64.78, 1.1) * mm});
            skLineSegment(sketch, "E678", {"start": v(64.78, 1.1) * mm, "end": v(64.87, 1.13) * mm});
            skLineSegment(sketch, "E679", {"start": v(64.87, 1.13) * mm, "end": v(64.96, 1.16) * mm});
            skLineSegment(sketch, "E680", {"start": v(64.96, 1.16) * mm, "end": v(65.05, 1.19) * mm});
            skLineSegment(sketch, "E681", {"start": v(65.05, 1.19) * mm, "end": v(65.14, 1.22) * mm});
            skLineSegment(sketch, "E682", {"start": v(65.14, 1.22) * mm, "end": v(65.22, 1.26) * mm});
            skLineSegment(sketch, "E683", {"start": v(65.22, 1.26) * mm, "end": v(65.3, 1.3) * mm});
            skLineSegment(sketch, "E684", {"start": v(65.3, 1.3) * mm, "end": v(65.39, 1.35) * mm});
            skLineSegment(sketch, "E685", {"start": v(65.39, 1.35) * mm, "end": v(65.47, 1.4) * mm});
            skLineSegment(sketch, "E686", {"start": v(65.47, 1.4) * mm, "end": v(65.54, 1.45) * mm});
            skLineSegment(sketch, "E687", {"start": v(65.54, 1.45) * mm, "end": v(65.62, 1.51) * mm});
            skLineSegment(sketch, "E688", {"start": v(65.62, 1.51) * mm, "end": v(65.69, 1.57) * mm});
            skLineSegment(sketch, "E689", {"start": v(65.69, 1.57) * mm, "end": v(65.75, 1.64) * mm});
            skLineSegment(sketch, "E690", {"start": v(65.75, 1.64) * mm, "end": v(65.82, 1.7) * mm});
            skLineSegment(sketch, "E691", {"start": v(65.82, 1.7) * mm, "end": v(65.88, 1.77) * mm});
            skLineSegment(sketch, "E692", {"start": v(65.88, 1.77) * mm, "end": v(65.93, 1.85) * mm});
            skLineSegment(sketch, "E693", {"start": v(65.93, 1.85) * mm, "end": v(65.99, 1.92) * mm});
            skLineSegment(sketch, "E694", {"start": v(65.99, 1.92) * mm, "end": v(66.04, 2) * mm});
            skLineSegment(sketch, "E695", {"start": v(66.04, 2) * mm, "end": v(66.08, 2.08) * mm});
            skLineSegment(sketch, "E696", {"start": v(66.08, 2.08) * mm, "end": v(66.13, 2.16) * mm});
            skLineSegment(sketch, "E697", {"start": v(66.13, 2.16) * mm, "end": v(66.17, 2.25) * mm});
            skLineSegment(sketch, "E698", {"start": v(66.17, 2.25) * mm, "end": v(66.2, 2.34) * mm});
            skLineSegment(sketch, "E699", {"start": v(66.2, 2.34) * mm, "end": v(66.23, 2.43) * mm});
            skLineSegment(sketch, "E700", {"start": v(66.23, 2.43) * mm, "end": v(66.26, 2.52) * mm});
            skLineSegment(sketch, "E701", {"start": v(66.26, 2.52) * mm, "end": v(66.28, 2.61) * mm});
            skLineSegment(sketch, "E702", {"start": v(66.28, 2.61) * mm, "end": v(66.3, 2.7) * mm});
            skLineSegment(sketch, "E703", {"start": v(66.3, 2.7) * mm, "end": v(66.3, 2.8) * mm});
            skLineSegment(sketch, "E704", {"start": v(66.3, 2.8) * mm, "end": v(66.32, 2.9) * mm});
            skLineSegment(sketch, "E705", {"start": v(66.32, 2.9) * mm, "end": v(66.32, 3) * mm});
            skLineSegment(sketch, "E706", {"start": v(66.32, 3) * mm, "end": v(66.32, 3.1) * mm});
            skLineSegment(sketch, "E707", {"start": v(-13.3, -0.97) * mm, "end": v(-13.37, -1.93) * mm});
            skLineSegment(sketch, "E708", {"start": v(-13.37, -1.93) * mm, "end": v(-13.49, -2.88) * mm});
            skLineSegment(sketch, "E709", {"start": v(-13.49, -2.88) * mm, "end": v(-13.65, -3.8) * mm});
            skLineSegment(sketch, "E710", {"start": v(-13.65, -3.8) * mm, "end": v(-13.86, -4.72) * mm});
            skLineSegment(sketch, "E711", {"start": v(-13.86, -4.72) * mm, "end": v(-14.12, -5.62) * mm});
            skLineSegment(sketch, "E712", {"start": v(-14.12, -5.62) * mm, "end": v(-14.42, -6.5) * mm});
            skLineSegment(sketch, "E713", {"start": v(-14.42, -6.5) * mm, "end": v(-14.76, -7.36) * mm});
            skLineSegment(sketch, "E714", {"start": v(-14.76, -7.36) * mm, "end": v(-15.14, -8.2) * mm});
            skLineSegment(sketch, "E715", {"start": v(-15.14, -8.2) * mm, "end": v(-15.55, -9) * mm});
            skLineSegment(sketch, "E716", {"start": v(-15.55, -9) * mm, "end": v(-16.01, -9.8) * mm});
            skLineSegment(sketch, "E717", {"start": v(-16.01, -9.8) * mm, "end": v(-16.5, -10.57) * mm});
            skLineSegment(sketch, "E718", {"start": v(-16.5, -10.57) * mm, "end": v(-17.03, -11.31) * mm});
            skLineSegment(sketch, "E719", {"start": v(-17.03, -11.31) * mm, "end": v(-17.6, -12.03) * mm});
            skLineSegment(sketch, "E720", {"start": v(-17.6, -12.03) * mm, "end": v(-18.19, -12.71) * mm});
            skLineSegment(sketch, "E721", {"start": v(-18.19, -12.71) * mm, "end": v(-18.81, -13.37) * mm});
            skLineSegment(sketch, "E722", {"start": v(-18.81, -13.37) * mm, "end": v(-19.47, -14) * mm});
            skLineSegment(sketch, "E723", {"start": v(-19.47, -14) * mm, "end": v(-20.16, -14.6) * mm});
            skLineSegment(sketch, "E724", {"start": v(-20.16, -14.6) * mm, "end": v(-20.87, -15.15) * mm});
            skLineSegment(sketch, "E725", {"start": v(-20.87, -15.15) * mm, "end": v(-21.62, -15.68) * mm});
            skLineSegment(sketch, "E726", {"start": v(-21.62, -15.68) * mm, "end": v(-22.38, -16.17) * mm});
            skLineSegment(sketch, "E727", {"start": v(-22.38, -16.17) * mm, "end": v(-23.18, -16.63) * mm});
            skLineSegment(sketch, "E728", {"start": v(-23.18, -16.63) * mm, "end": v(-24, -17.05) * mm});
            skLineSegment(sketch, "E729", {"start": v(-24, -17.05) * mm, "end": v(-24.83, -17.43) * mm});
            skLineSegment(sketch, "E730", {"start": v(-24.83, -17.43) * mm, "end": v(-25.69, -17.77) * mm});
            skLineSegment(sketch, "E731", {"start": v(-25.69, -17.77) * mm, "end": v(-26.57, -18.07) * mm});
            skLineSegment(sketch, "E732", {"start": v(-26.57, -18.07) * mm, "end": v(-27.46, -18.32) * mm});
            skLineSegment(sketch, "E733", {"start": v(-27.46, -18.32) * mm, "end": v(-28.38, -18.53) * mm});
            skLineSegment(sketch, "E734", {"start": v(-28.38, -18.53) * mm, "end": v(-29.3, -18.7) * mm});
            skLineSegment(sketch, "E735", {"start": v(-29.3, -18.7) * mm, "end": v(-30.25, -18.82) * mm});
            skLineSegment(sketch, "E736", {"start": v(-30.25, -18.82) * mm, "end": v(-31.21, -18.9) * mm});
            skLineSegment(sketch, "E737", {"start": v(-31.21, -18.9) * mm, "end": v(-32.19, -18.92) * mm});
            skLineSegment(sketch, "E738", {"start": v(-32.19, -18.92) * mm, "end": v(-33.16, -18.9) * mm});
            skLineSegment(sketch, "E739", {"start": v(-33.16, -18.9) * mm, "end": v(-34.12, -18.82) * mm});
            skLineSegment(sketch, "E740", {"start": v(-34.12, -18.82) * mm, "end": v(-35.06, -18.7) * mm});
            skLineSegment(sketch, "E741", {"start": v(-35.06, -18.7) * mm, "end": v(-36, -18.53) * mm});
            skLineSegment(sketch, "E742", {"start": v(-36, -18.53) * mm, "end": v(-36.9, -18.32) * mm});
            skLineSegment(sketch, "E743", {"start": v(-36.9, -18.32) * mm, "end": v(-37.8, -18.07) * mm});
            skLineSegment(sketch, "E744", {"start": v(-37.8, -18.07) * mm, "end": v(-38.68, -17.77) * mm});
            skLineSegment(sketch, "E745", {"start": v(-38.68, -17.77) * mm, "end": v(-39.54, -17.43) * mm});
            skLineSegment(sketch, "E746", {"start": v(-39.54, -17.43) * mm, "end": v(-40.38, -17.05) * mm});
            skLineSegment(sketch, "E747", {"start": v(-40.38, -17.05) * mm, "end": v(-41.2, -16.63) * mm});
            skLineSegment(sketch, "E748", {"start": v(-41.2, -16.63) * mm, "end": v(-41.99, -16.17) * mm});
            skLineSegment(sketch, "E749", {"start": v(-41.99, -16.17) * mm, "end": v(-42.75, -15.68) * mm});
            skLineSegment(sketch, "E750", {"start": v(-42.75, -15.68) * mm, "end": v(-43.5, -15.15) * mm});
            skLineSegment(sketch, "E751", {"start": v(-43.5, -15.15) * mm, "end": v(-44.21, -14.6) * mm});
            skLineSegment(sketch, "E752", {"start": v(-44.21, -14.6) * mm, "end": v(-44.9, -14) * mm});
            skLineSegment(sketch, "E753", {"start": v(-44.9, -14) * mm, "end": v(-45.56, -13.37) * mm});
            skLineSegment(sketch, "E754", {"start": v(-45.56, -13.37) * mm, "end": v(-46.18, -12.71) * mm});
            skLineSegment(sketch, "E755", {"start": v(-46.18, -12.71) * mm, "end": v(-46.78, -12.03) * mm});
            skLineSegment(sketch, "E756", {"start": v(-46.78, -12.03) * mm, "end": v(-47.34, -11.31) * mm});
            skLineSegment(sketch, "E757", {"start": v(-47.34, -11.31) * mm, "end": v(-47.87, -10.57) * mm});
            skLineSegment(sketch, "E758", {"start": v(-47.87, -10.57) * mm, "end": v(-48.36, -9.8) * mm});
            skLineSegment(sketch, "E759", {"start": v(-48.36, -9.8) * mm, "end": v(-48.82, -9) * mm});
            skLineSegment(sketch, "E760", {"start": v(-48.82, -9) * mm, "end": v(-49.23, -8.2) * mm});
            skLineSegment(sketch, "E761", {"start": v(-49.23, -8.2) * mm, "end": v(-49.61, -7.36) * mm});
            skLineSegment(sketch, "E762", {"start": v(-49.61, -7.36) * mm, "end": v(-49.95, -6.5) * mm});
            skLineSegment(sketch, "E763", {"start": v(-49.95, -6.5) * mm, "end": v(-50.25, -5.62) * mm});
            skLineSegment(sketch, "E764", {"start": v(-50.25, -5.62) * mm, "end": v(-50.5, -4.72) * mm});
            skLineSegment(sketch, "E765", {"start": v(-50.5, -4.72) * mm, "end": v(-50.72, -3.8) * mm});
            skLineSegment(sketch, "E766", {"start": v(-50.72, -3.8) * mm, "end": v(-50.88, -2.88) * mm});
            skLineSegment(sketch, "E767", {"start": v(-50.88, -2.88) * mm, "end": v(-51, -1.93) * mm});
            skLineSegment(sketch, "E768", {"start": v(-51, -1.93) * mm, "end": v(-51.08, -0.97) * mm});
            skLineSegment(sketch, "E769", {"start": v(-51.08, -0.97) * mm, "end": v(-51.1, 0) * mm});
            skLineSegment(sketch, "E770", {"start": v(-51.1, 0) * mm, "end": v(-51.08, 0.97) * mm});
            skLineSegment(sketch, "E771", {"start": v(-51.08, 0.97) * mm, "end": v(-51, 1.93) * mm});
            skLineSegment(sketch, "E772", {"start": v(-51, 1.93) * mm, "end": v(-50.88, 2.88) * mm});
            skLineSegment(sketch, "E773", {"start": v(-50.88, 2.88) * mm, "end": v(-50.72, 3.8) * mm});
            skLineSegment(sketch, "E774", {"start": v(-50.72, 3.8) * mm, "end": v(-50.5, 4.72) * mm});
            skLineSegment(sketch, "E775", {"start": v(-50.5, 4.72) * mm, "end": v(-50.25, 5.62) * mm});
            skLineSegment(sketch, "E776", {"start": v(-50.25, 5.62) * mm, "end": v(-49.95, 6.5) * mm});
            skLineSegment(sketch, "E777", {"start": v(-49.95, 6.5) * mm, "end": v(-49.61, 7.36) * mm});
            skLineSegment(sketch, "E778", {"start": v(-49.61, 7.36) * mm, "end": v(-49.23, 8.2) * mm});
            skLineSegment(sketch, "E779", {"start": v(-49.23, 8.2) * mm, "end": v(-48.82, 9) * mm});
            skLineSegment(sketch, "E780", {"start": v(-48.82, 9) * mm, "end": v(-48.36, 9.8) * mm});
            skLineSegment(sketch, "E781", {"start": v(-48.36, 9.8) * mm, "end": v(-47.87, 10.57) * mm});
            skLineSegment(sketch, "E782", {"start": v(-47.87, 10.57) * mm, "end": v(-47.34, 11.31) * mm});
            skLineSegment(sketch, "E783", {"start": v(-47.34, 11.31) * mm, "end": v(-46.78, 12.03) * mm});
            skLineSegment(sketch, "E784", {"start": v(-46.78, 12.03) * mm, "end": v(-46.18, 12.71) * mm});
            skLineSegment(sketch, "E785", {"start": v(-46.18, 12.71) * mm, "end": v(-45.56, 13.37) * mm});
            skLineSegment(sketch, "E786", {"start": v(-45.56, 13.37) * mm, "end": v(-44.9, 14) * mm});
            skLineSegment(sketch, "E787", {"start": v(-44.9, 14) * mm, "end": v(-44.21, 14.6) * mm});
            skLineSegment(sketch, "E788", {"start": v(-44.21, 14.6) * mm, "end": v(-43.5, 15.15) * mm});
            skLineSegment(sketch, "E789", {"start": v(-43.5, 15.15) * mm, "end": v(-42.75, 15.68) * mm});
            skLineSegment(sketch, "E790", {"start": v(-42.75, 15.68) * mm, "end": v(-41.99, 16.17) * mm});
            skLineSegment(sketch, "E791", {"start": v(-41.99, 16.17) * mm, "end": v(-41.2, 16.63) * mm});
            skLineSegment(sketch, "E792", {"start": v(-41.2, 16.63) * mm, "end": v(-40.38, 17.05) * mm});
            skLineSegment(sketch, "E793", {"start": v(-40.38, 17.05) * mm, "end": v(-39.54, 17.43) * mm});
            skLineSegment(sketch, "E794", {"start": v(-39.54, 17.43) * mm, "end": v(-38.68, 17.77) * mm});
            skLineSegment(sketch, "E795", {"start": v(-38.68, 17.77) * mm, "end": v(-37.8, 18.07) * mm});
            skLineSegment(sketch, "E796", {"start": v(-37.8, 18.07) * mm, "end": v(-36.9, 18.32) * mm});
            skLineSegment(sketch, "E797", {"start": v(-36.9, 18.32) * mm, "end": v(-36, 18.53) * mm});
            skLineSegment(sketch, "E798", {"start": v(-36, 18.53) * mm, "end": v(-35.06, 18.7) * mm});
            skLineSegment(sketch, "E799", {"start": v(-35.06, 18.7) * mm, "end": v(-34.12, 18.82) * mm});
            skLineSegment(sketch, "E800", {"start": v(-34.12, 18.82) * mm, "end": v(-33.16, 18.9) * mm});
            skLineSegment(sketch, "E801", {"start": v(-33.16, 18.9) * mm, "end": v(-32.19, 18.92) * mm});
            skLineSegment(sketch, "E802", {"start": v(-32.19, 18.92) * mm, "end": v(-31.21, 18.9) * mm});
            skLineSegment(sketch, "E803", {"start": v(-31.21, 18.9) * mm, "end": v(-30.25, 18.82) * mm});
            skLineSegment(sketch, "E804", {"start": v(-30.25, 18.82) * mm, "end": v(-29.3, 18.7) * mm});
            skLineSegment(sketch, "E805", {"start": v(-29.3, 18.7) * mm, "end": v(-28.38, 18.53) * mm});
            skLineSegment(sketch, "E806", {"start": v(-28.38, 18.53) * mm, "end": v(-27.46, 18.32) * mm});
            skLineSegment(sketch, "E807", {"start": v(-27.46, 18.32) * mm, "end": v(-26.57, 18.07) * mm});
            skLineSegment(sketch, "E808", {"start": v(-26.57, 18.07) * mm, "end": v(-25.69, 17.77) * mm});
            skLineSegment(sketch, "E809", {"start": v(-25.69, 17.77) * mm, "end": v(-24.83, 17.43) * mm});
            skLineSegment(sketch, "E810", {"start": v(-24.83, 17.43) * mm, "end": v(-24, 17.05) * mm});
            skLineSegment(sketch, "E811", {"start": v(-24, 17.05) * mm, "end": v(-23.18, 16.63) * mm});
            skLineSegment(sketch, "E812", {"start": v(-23.18, 16.63) * mm, "end": v(-22.38, 16.17) * mm});
            skLineSegment(sketch, "E813", {"start": v(-22.38, 16.17) * mm, "end": v(-21.62, 15.68) * mm});
            skLineSegment(sketch, "E814", {"start": v(-21.62, 15.68) * mm, "end": v(-20.87, 15.15) * mm});
            skLineSegment(sketch, "E815", {"start": v(-20.87, 15.15) * mm, "end": v(-20.16, 14.6) * mm});
            skLineSegment(sketch, "E816", {"start": v(-20.16, 14.6) * mm, "end": v(-19.47, 14) * mm});
            skLineSegment(sketch, "E817", {"start": v(-19.47, 14) * mm, "end": v(-18.81, 13.37) * mm});
            skLineSegment(sketch, "E818", {"start": v(-18.81, 13.37) * mm, "end": v(-18.19, 12.71) * mm});
            skLineSegment(sketch, "E819", {"start": v(-18.19, 12.71) * mm, "end": v(-17.6, 12.03) * mm});
            skLineSegment(sketch, "E820", {"start": v(-17.6, 12.03) * mm, "end": v(-17.03, 11.31) * mm});
            skLineSegment(sketch, "E821", {"start": v(-17.03, 11.31) * mm, "end": v(-16.5, 10.57) * mm});
            skLineSegment(sketch, "E822", {"start": v(-16.5, 10.57) * mm, "end": v(-16.01, 9.8) * mm});
            skLineSegment(sketch, "E823", {"start": v(-16.01, 9.8) * mm, "end": v(-15.55, 9) * mm});
            skLineSegment(sketch, "E824", {"start": v(-15.55, 9) * mm, "end": v(-15.14, 8.2) * mm});
            skLineSegment(sketch, "E825", {"start": v(-15.14, 8.2) * mm, "end": v(-14.76, 7.36) * mm});
            skLineSegment(sketch, "E826", {"start": v(-14.76, 7.36) * mm, "end": v(-14.42, 6.5) * mm});
            skLineSegment(sketch, "E827", {"start": v(-14.42, 6.5) * mm, "end": v(-14.12, 5.62) * mm});
            skLineSegment(sketch, "E828", {"start": v(-14.12, 5.62) * mm, "end": v(-13.86, 4.72) * mm});
            skLineSegment(sketch, "E829", {"start": v(-13.86, 4.72) * mm, "end": v(-13.65, 3.8) * mm});
            skLineSegment(sketch, "E830", {"start": v(-13.65, 3.8) * mm, "end": v(-13.49, 2.88) * mm});
            skLineSegment(sketch, "E831", {"start": v(-13.49, 2.88) * mm, "end": v(-13.37, 1.93) * mm});
            skLineSegment(sketch, "E832", {"start": v(-13.37, 1.93) * mm, "end": v(-13.3, 0.97) * mm});
            skLineSegment(sketch, "E833", {"start": v(-13.3, 0.97) * mm, "end": v(-13.27, 0) * mm});
            skLineSegment(sketch, "E834", {"start": v(-13.27, 0) * mm, "end": v(-13.3, -0.97) * mm});
            skLineSegment(sketch, "E835", {"start": v(-8.18, 4.22) * mm, "end": v(-8.27, 3.92) * mm});
            skLineSegment(sketch, "E836", {"start": v(-8.27, 3.92) * mm, "end": v(-8.42, 3.65) * mm});
            skLineSegment(sketch, "E837", {"start": v(-8.42, 3.65) * mm, "end": v(-8.62, 3.41) * mm});
            skLineSegment(sketch, "E838", {"start": v(-8.62, 3.41) * mm, "end": v(-8.85, 3.21) * mm});
            skLineSegment(sketch, "E839", {"start": v(-8.85, 3.21) * mm, "end": v(-9.13, 3.07) * mm});
            skLineSegment(sketch, "E840", {"start": v(-9.13, 3.07) * mm, "end": v(-9.43, 2.97) * mm});
            skLineSegment(sketch, "E841", {"start": v(-9.43, 2.97) * mm, "end": v(-9.75, 2.94) * mm});
            skLineSegment(sketch, "E842", {"start": v(-9.75, 2.94) * mm, "end": v(-10.07, 2.97) * mm});
            skLineSegment(sketch, "E843", {"start": v(-10.07, 2.97) * mm, "end": v(-10.37, 3.07) * mm});
            skLineSegment(sketch, "E844", {"start": v(-10.37, 3.07) * mm, "end": v(-10.64, 3.21) * mm});
            skLineSegment(sketch, "E845", {"start": v(-10.64, 3.21) * mm, "end": v(-10.88, 3.41) * mm});
            skLineSegment(sketch, "E846", {"start": v(-10.88, 3.41) * mm, "end": v(-11.08, 3.65) * mm});
            skLineSegment(sketch, "E847", {"start": v(-11.08, 3.65) * mm, "end": v(-11.22, 3.92) * mm});
            skLineSegment(sketch, "E848", {"start": v(-11.22, 3.92) * mm, "end": v(-11.32, 4.22) * mm});
            skLineSegment(sketch, "E849", {"start": v(-11.32, 4.22) * mm, "end": v(-11.35, 4.54) * mm});
            skLineSegment(sketch, "E850", {"start": v(-11.35, 4.54) * mm, "end": v(-11.32, 4.86) * mm});
            skLineSegment(sketch, "E851", {"start": v(-11.32, 4.86) * mm, "end": v(-11.22, 5.16) * mm});
            skLineSegment(sketch, "E852", {"start": v(-11.22, 5.16) * mm, "end": v(-11.08, 5.44) * mm});
            skLineSegment(sketch, "E853", {"start": v(-11.08, 5.44) * mm, "end": v(-10.88, 5.67) * mm});
            skLineSegment(sketch, "E854", {"start": v(-10.88, 5.67) * mm, "end": v(-10.64, 5.87) * mm});
            skLineSegment(sketch, "E855", {"start": v(-10.64, 5.87) * mm, "end": v(-10.37, 6.02) * mm});
            skLineSegment(sketch, "E856", {"start": v(-10.37, 6.02) * mm, "end": v(-10.07, 6.1) * mm});
            skLineSegment(sketch, "E857", {"start": v(-10.07, 6.1) * mm, "end": v(-9.75, 6.14) * mm});
            skLineSegment(sketch, "E858", {"start": v(-9.75, 6.14) * mm, "end": v(-9.43, 6.1) * mm});
            skLineSegment(sketch, "E859", {"start": v(-9.43, 6.1) * mm, "end": v(-9.13, 6.02) * mm});
            skLineSegment(sketch, "E860", {"start": v(-9.13, 6.02) * mm, "end": v(-8.85, 5.87) * mm});
            skLineSegment(sketch, "E861", {"start": v(-8.85, 5.87) * mm, "end": v(-8.62, 5.67) * mm});
            skLineSegment(sketch, "E862", {"start": v(-8.62, 5.67) * mm, "end": v(-8.42, 5.44) * mm});
            skLineSegment(sketch, "E863", {"start": v(-8.42, 5.44) * mm, "end": v(-8.27, 5.16) * mm});
            skLineSegment(sketch, "E864", {"start": v(-8.27, 5.16) * mm, "end": v(-8.18, 4.86) * mm});
            skLineSegment(sketch, "E865", {"start": v(-8.18, 4.86) * mm, "end": v(-8.15, 4.54) * mm});
            skLineSegment(sketch, "E866", {"start": v(-8.15, 4.54) * mm, "end": v(-8.18, 4.22) * mm});
            skLineSegment(sketch, "E867", {"start": v(51.08, -0.97) * mm, "end": v(51, -1.93) * mm});
            skLineSegment(sketch, "E868", {"start": v(51, -1.93) * mm, "end": v(50.88, -2.88) * mm});
            skLineSegment(sketch, "E869", {"start": v(50.88, -2.88) * mm, "end": v(50.72, -3.8) * mm});
            skLineSegment(sketch, "E870", {"start": v(50.72, -3.8) * mm, "end": v(50.5, -4.72) * mm});
            skLineSegment(sketch, "E871", {"start": v(50.5, -4.72) * mm, "end": v(50.25, -5.62) * mm});
            skLineSegment(sketch, "E872", {"start": v(50.25, -5.62) * mm, "end": v(49.95, -6.5) * mm});
            skLineSegment(sketch, "E873", {"start": v(49.95, -6.5) * mm, "end": v(49.61, -7.36) * mm});
            skLineSegment(sketch, "E874", {"start": v(49.61, -7.36) * mm, "end": v(49.23, -8.2) * mm});
            skLineSegment(sketch, "E875", {"start": v(49.23, -8.2) * mm, "end": v(48.82, -9) * mm});
            skLineSegment(sketch, "E876", {"start": v(48.82, -9) * mm, "end": v(48.36, -9.8) * mm});
            skLineSegment(sketch, "E877", {"start": v(48.36, -9.8) * mm, "end": v(47.87, -10.57) * mm});
            skLineSegment(sketch, "E878", {"start": v(47.87, -10.57) * mm, "end": v(47.34, -11.31) * mm});
            skLineSegment(sketch, "E879", {"start": v(47.34, -11.31) * mm, "end": v(46.78, -12.03) * mm});
            skLineSegment(sketch, "E880", {"start": v(46.78, -12.03) * mm, "end": v(46.18, -12.71) * mm});
            skLineSegment(sketch, "E881", {"start": v(46.18, -12.71) * mm, "end": v(45.56, -13.37) * mm});
            skLineSegment(sketch, "E882", {"start": v(45.56, -13.37) * mm, "end": v(44.9, -14) * mm});
            skLineSegment(sketch, "E883", {"start": v(44.9, -14) * mm, "end": v(44.21, -14.6) * mm});
            skLineSegment(sketch, "E884", {"start": v(44.21, -14.6) * mm, "end": v(43.5, -15.15) * mm});
            skLineSegment(sketch, "E885", {"start": v(43.5, -15.15) * mm, "end": v(42.76, -15.68) * mm});
            skLineSegment(sketch, "E886", {"start": v(42.76, -15.68) * mm, "end": v(41.99, -16.17) * mm});
            skLineSegment(sketch, "E887", {"start": v(41.99, -16.17) * mm, "end": v(41.2, -16.63) * mm});
            skLineSegment(sketch, "E888", {"start": v(41.2, -16.63) * mm, "end": v(40.38, -17.05) * mm});
            skLineSegment(sketch, "E889", {"start": v(40.38, -17.05) * mm, "end": v(39.54, -17.43) * mm});
            skLineSegment(sketch, "E890", {"start": v(39.54, -17.43) * mm, "end": v(38.68, -17.77) * mm});
            skLineSegment(sketch, "E891", {"start": v(38.68, -17.77) * mm, "end": v(37.8, -18.07) * mm});
            skLineSegment(sketch, "E892", {"start": v(37.8, -18.07) * mm, "end": v(36.9, -18.32) * mm});
            skLineSegment(sketch, "E893", {"start": v(36.9, -18.32) * mm, "end": v(36, -18.53) * mm});
            skLineSegment(sketch, "E894", {"start": v(36, -18.53) * mm, "end": v(35.06, -18.7) * mm});
            skLineSegment(sketch, "E895", {"start": v(35.06, -18.7) * mm, "end": v(34.12, -18.82) * mm});
            skLineSegment(sketch, "E896", {"start": v(34.12, -18.82) * mm, "end": v(33.16, -18.9) * mm});
            skLineSegment(sketch, "E897", {"start": v(33.16, -18.9) * mm, "end": v(32.19, -18.92) * mm});
            skLineSegment(sketch, "E898", {"start": v(32.19, -18.92) * mm, "end": v(31.21, -18.9) * mm});
            skLineSegment(sketch, "E899", {"start": v(31.21, -18.9) * mm, "end": v(30.25, -18.82) * mm});
            skLineSegment(sketch, "E900", {"start": v(30.25, -18.82) * mm, "end": v(29.3, -18.7) * mm});
            skLineSegment(sketch, "E901", {"start": v(29.3, -18.7) * mm, "end": v(28.38, -18.53) * mm});
            skLineSegment(sketch, "E902", {"start": v(28.38, -18.53) * mm, "end": v(27.46, -18.32) * mm});
            skLineSegment(sketch, "E903", {"start": v(27.46, -18.32) * mm, "end": v(26.57, -18.07) * mm});
            skLineSegment(sketch, "E904", {"start": v(26.57, -18.07) * mm, "end": v(25.69, -17.77) * mm});
            skLineSegment(sketch, "E905", {"start": v(25.69, -17.77) * mm, "end": v(24.83, -17.43) * mm});
            skLineSegment(sketch, "E906", {"start": v(24.83, -17.43) * mm, "end": v(24, -17.05) * mm});
            skLineSegment(sketch, "E907", {"start": v(24, -17.05) * mm, "end": v(23.18, -16.63) * mm});
            skLineSegment(sketch, "E908", {"start": v(23.18, -16.63) * mm, "end": v(22.38, -16.17) * mm});
            skLineSegment(sketch, "E909", {"start": v(22.38, -16.17) * mm, "end": v(21.62, -15.68) * mm});
            skLineSegment(sketch, "E910", {"start": v(21.62, -15.68) * mm, "end": v(20.87, -15.15) * mm});
            skLineSegment(sketch, "E911", {"start": v(20.87, -15.15) * mm, "end": v(20.16, -14.6) * mm});
            skLineSegment(sketch, "E912", {"start": v(20.16, -14.6) * mm, "end": v(19.47, -14) * mm});
            skLineSegment(sketch, "E913", {"start": v(19.47, -14) * mm, "end": v(18.82, -13.37) * mm});
            skLineSegment(sketch, "E914", {"start": v(18.82, -13.37) * mm, "end": v(18.19, -12.71) * mm});
            skLineSegment(sketch, "E915", {"start": v(18.19, -12.71) * mm, "end": v(17.6, -12.03) * mm});
            skLineSegment(sketch, "E916", {"start": v(17.6, -12.03) * mm, "end": v(17.03, -11.31) * mm});
            skLineSegment(sketch, "E917", {"start": v(17.03, -11.31) * mm, "end": v(16.5, -10.57) * mm});
            skLineSegment(sketch, "E918", {"start": v(16.5, -10.57) * mm, "end": v(16.01, -9.8) * mm});
            skLineSegment(sketch, "E919", {"start": v(16.01, -9.8) * mm, "end": v(15.55, -9) * mm});
            skLineSegment(sketch, "E920", {"start": v(15.55, -9) * mm, "end": v(15.14, -8.2) * mm});
            skLineSegment(sketch, "E921", {"start": v(15.14, -8.2) * mm, "end": v(14.76, -7.36) * mm});
            skLineSegment(sketch, "E922", {"start": v(14.76, -7.36) * mm, "end": v(14.42, -6.5) * mm});
            skLineSegment(sketch, "E923", {"start": v(14.42, -6.5) * mm, "end": v(14.12, -5.62) * mm});
            skLineSegment(sketch, "E924", {"start": v(14.12, -5.62) * mm, "end": v(13.86, -4.72) * mm});
            skLineSegment(sketch, "E925", {"start": v(13.86, -4.72) * mm, "end": v(13.65, -3.8) * mm});
            skLineSegment(sketch, "E926", {"start": v(13.65, -3.8) * mm, "end": v(13.49, -2.88) * mm});
            skLineSegment(sketch, "E927", {"start": v(13.49, -2.88) * mm, "end": v(13.37, -1.93) * mm});
            skLineSegment(sketch, "E928", {"start": v(13.37, -1.93) * mm, "end": v(13.3, -0.97) * mm});
            skLineSegment(sketch, "E929", {"start": v(13.3, -0.97) * mm, "end": v(13.27, 0) * mm});
            skLineSegment(sketch, "E930", {"start": v(13.27, 0) * mm, "end": v(13.3, 0.97) * mm});
            skLineSegment(sketch, "E931", {"start": v(13.3, 0.97) * mm, "end": v(13.37, 1.93) * mm});
            skLineSegment(sketch, "E932", {"start": v(13.37, 1.93) * mm, "end": v(13.49, 2.88) * mm});
            skLineSegment(sketch, "E933", {"start": v(13.49, 2.88) * mm, "end": v(13.65, 3.8) * mm});
            skLineSegment(sketch, "E934", {"start": v(13.65, 3.8) * mm, "end": v(13.86, 4.72) * mm});
            skLineSegment(sketch, "E935", {"start": v(13.86, 4.72) * mm, "end": v(14.12, 5.62) * mm});
            skLineSegment(sketch, "E936", {"start": v(14.12, 5.62) * mm, "end": v(14.42, 6.5) * mm});
            skLineSegment(sketch, "E937", {"start": v(14.42, 6.5) * mm, "end": v(14.76, 7.36) * mm});
            skLineSegment(sketch, "E938", {"start": v(14.76, 7.36) * mm, "end": v(15.14, 8.2) * mm});
            skLineSegment(sketch, "E939", {"start": v(15.14, 8.2) * mm, "end": v(15.55, 9) * mm});
            skLineSegment(sketch, "E940", {"start": v(15.55, 9) * mm, "end": v(16.01, 9.8) * mm});
            skLineSegment(sketch, "E941", {"start": v(16.01, 9.8) * mm, "end": v(16.5, 10.57) * mm});
            skLineSegment(sketch, "E942", {"start": v(16.5, 10.57) * mm, "end": v(17.03, 11.31) * mm});
            skLineSegment(sketch, "E943", {"start": v(17.03, 11.31) * mm, "end": v(17.6, 12.03) * mm});
            skLineSegment(sketch, "E944", {"start": v(17.6, 12.03) * mm, "end": v(18.19, 12.71) * mm});
            skLineSegment(sketch, "E945", {"start": v(18.19, 12.71) * mm, "end": v(18.82, 13.37) * mm});
            skLineSegment(sketch, "E946", {"start": v(18.82, 13.37) * mm, "end": v(19.47, 14) * mm});
            skLineSegment(sketch, "E947", {"start": v(19.47, 14) * mm, "end": v(20.16, 14.6) * mm});
            skLineSegment(sketch, "E948", {"start": v(20.16, 14.6) * mm, "end": v(20.87, 15.15) * mm});
            skLineSegment(sketch, "E949", {"start": v(20.87, 15.15) * mm, "end": v(21.62, 15.68) * mm});
            skLineSegment(sketch, "E950", {"start": v(21.62, 15.68) * mm, "end": v(22.38, 16.17) * mm});
            skLineSegment(sketch, "E951", {"start": v(22.38, 16.17) * mm, "end": v(23.18, 16.63) * mm});
            skLineSegment(sketch, "E952", {"start": v(23.18, 16.63) * mm, "end": v(24, 17.05) * mm});
            skLineSegment(sketch, "E953", {"start": v(24, 17.05) * mm, "end": v(24.83, 17.43) * mm});
            skLineSegment(sketch, "E954", {"start": v(24.83, 17.43) * mm, "end": v(25.69, 17.77) * mm});
            skLineSegment(sketch, "E955", {"start": v(25.69, 17.77) * mm, "end": v(26.57, 18.07) * mm});
            skLineSegment(sketch, "E956", {"start": v(26.57, 18.07) * mm, "end": v(27.46, 18.32) * mm});
            skLineSegment(sketch, "E957", {"start": v(27.46, 18.32) * mm, "end": v(28.38, 18.53) * mm});
            skLineSegment(sketch, "E958", {"start": v(28.38, 18.53) * mm, "end": v(29.3, 18.7) * mm});
            skLineSegment(sketch, "E959", {"start": v(29.3, 18.7) * mm, "end": v(30.25, 18.82) * mm});
            skLineSegment(sketch, "E960", {"start": v(30.25, 18.82) * mm, "end": v(31.21, 18.9) * mm});
            skLineSegment(sketch, "E961", {"start": v(31.21, 18.9) * mm, "end": v(32.19, 18.92) * mm});
            skLineSegment(sketch, "E962", {"start": v(32.19, 18.92) * mm, "end": v(33.16, 18.9) * mm});
            skLineSegment(sketch, "E963", {"start": v(33.16, 18.9) * mm, "end": v(34.12, 18.82) * mm});
            skLineSegment(sketch, "E964", {"start": v(34.12, 18.82) * mm, "end": v(35.06, 18.7) * mm});
            skLineSegment(sketch, "E965", {"start": v(35.06, 18.7) * mm, "end": v(36, 18.53) * mm});
            skLineSegment(sketch, "E966", {"start": v(36, 18.53) * mm, "end": v(36.9, 18.32) * mm});
            skLineSegment(sketch, "E967", {"start": v(36.9, 18.32) * mm, "end": v(37.8, 18.07) * mm});
            skLineSegment(sketch, "E968", {"start": v(37.8, 18.07) * mm, "end": v(38.68, 17.77) * mm});
            skLineSegment(sketch, "E969", {"start": v(38.68, 17.77) * mm, "end": v(39.54, 17.43) * mm});
            skLineSegment(sketch, "E970", {"start": v(39.54, 17.43) * mm, "end": v(40.38, 17.05) * mm});
            skLineSegment(sketch, "E971", {"start": v(40.38, 17.05) * mm, "end": v(41.2, 16.63) * mm});
            skLineSegment(sketch, "E972", {"start": v(41.2, 16.63) * mm, "end": v(41.99, 16.17) * mm});
            skLineSegment(sketch, "E973", {"start": v(41.99, 16.17) * mm, "end": v(42.76, 15.68) * mm});
            skLineSegment(sketch, "E974", {"start": v(42.76, 15.68) * mm, "end": v(43.5, 15.15) * mm});
            skLineSegment(sketch, "E975", {"start": v(43.5, 15.15) * mm, "end": v(44.21, 14.6) * mm});
            skLineSegment(sketch, "E976", {"start": v(44.21, 14.6) * mm, "end": v(44.9, 14) * mm});
            skLineSegment(sketch, "E977", {"start": v(44.9, 14) * mm, "end": v(45.56, 13.37) * mm});
            skLineSegment(sketch, "E978", {"start": v(45.56, 13.37) * mm, "end": v(46.18, 12.71) * mm});
            skLineSegment(sketch, "E979", {"start": v(46.18, 12.71) * mm, "end": v(46.78, 12.03) * mm});
            skLineSegment(sketch, "E980", {"start": v(46.78, 12.03) * mm, "end": v(47.34, 11.31) * mm});
            skLineSegment(sketch, "E981", {"start": v(47.34, 11.31) * mm, "end": v(47.87, 10.57) * mm});
            skLineSegment(sketch, "E982", {"start": v(47.87, 10.57) * mm, "end": v(48.36, 9.8) * mm});
            skLineSegment(sketch, "E983", {"start": v(48.36, 9.8) * mm, "end": v(48.82, 9) * mm});
            skLineSegment(sketch, "E984", {"start": v(48.82, 9) * mm, "end": v(49.23, 8.2) * mm});
            skLineSegment(sketch, "E985", {"start": v(49.23, 8.2) * mm, "end": v(49.61, 7.36) * mm});
            skLineSegment(sketch, "E986", {"start": v(49.61, 7.36) * mm, "end": v(49.95, 6.5) * mm});
            skLineSegment(sketch, "E987", {"start": v(49.95, 6.5) * mm, "end": v(50.25, 5.62) * mm});
            skLineSegment(sketch, "E988", {"start": v(50.25, 5.62) * mm, "end": v(50.5, 4.72) * mm});
            skLineSegment(sketch, "E989", {"start": v(50.5, 4.72) * mm, "end": v(50.72, 3.8) * mm});
            skLineSegment(sketch, "E990", {"start": v(50.72, 3.8) * mm, "end": v(50.88, 2.88) * mm});
            skLineSegment(sketch, "E991", {"start": v(50.88, 2.88) * mm, "end": v(51, 1.93) * mm});
            skLineSegment(sketch, "E992", {"start": v(51, 1.93) * mm, "end": v(51.08, 0.97) * mm});
            skLineSegment(sketch, "E993", {"start": v(51.08, 0.97) * mm, "end": v(51.1, 0) * mm});
            skLineSegment(sketch, "E994", {"start": v(51.1, 0) * mm, "end": v(51.08, -0.97) * mm});
            skSolve(sketch);
        }
        {
            var Q0;
            Q0 = qSketchRegion(id + "F0", true);
            extrude(context, id + "F1", {"entities" : qUnion([Q0]), "depth" : 6 * mm, "offsetDistance" : 25 * mm});
        }
    });
